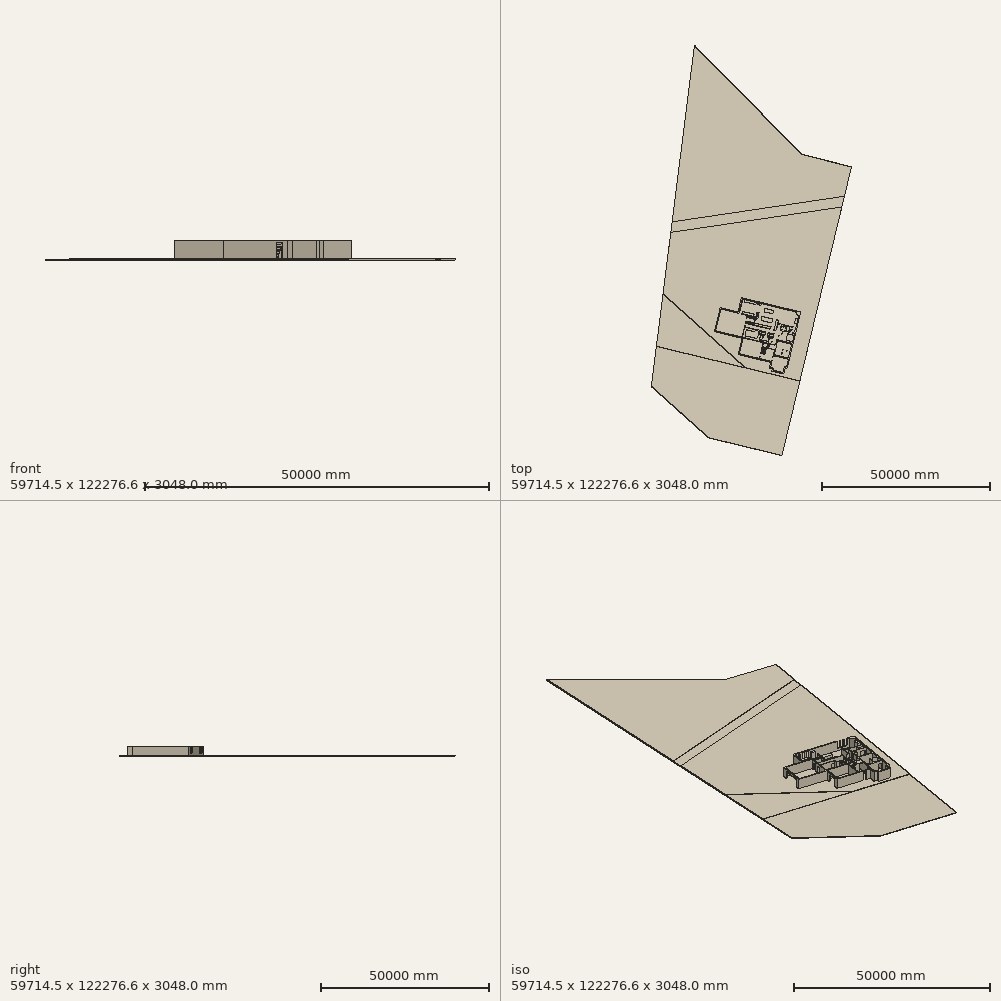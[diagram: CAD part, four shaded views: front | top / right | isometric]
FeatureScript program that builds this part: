
annotation { "Feature Type Name" : "Feature", "Feature Type Description" : "" }
export const myFeature = defineFeature(function(context is Context, id is Id, definition is map)
    precondition{}
    {
        {
            var Q0;
            Q0=qCreatedBy(makeId("Top.planeOp"),FACE);
            var sketch = newSketch(context, id + "F0", { "sketchPlane" : qUnion([Q0])});
            skLineSegment(sketch, "E0", {"start": v(0, 0) * mm, "end": v(31989.83, -32467.96) * mm});
            skLineSegment(sketch, "E1", {"start": v(31989.83, -32467.96) * mm, "end": v(46862.18, -36229.17) * mm});
            skLineSegment(sketch, "E2", {"start": v(46862.18, -36229.17) * mm, "end": v(26112.23, -122276.56) * mm});
            skLineSegment(sketch, "E3", {"start": v(46862.18, -36229.17) * mm, "end": v(46862.18, -51469.17) * mm, "construction": true});
            skLineSegment(sketch, "E4", {"start": v(0, 0) * mm, "end": v(-12852.3, -101676.89) * mm});
            skLineSegment(sketch, "E5", {"start": v(0, 0) * mm, "end": v(0, 15240) * mm, "construction": true});
            skLineSegment(sketch, "E6", {"start": v(26112.23, -122276.56) * mm, "end": v(4230, -116999.76) * mm});
            skLineSegment(sketch, "E7", {"start": v(26112.23, -122276.56) * mm, "end": v(10872.23, -122276.56) * mm, "construction": true});
            skLineSegment(sketch, "E8", {"start": v(4230, -116999.76) * mm, "end": v(-12852.3, -101676.89) * mm});
            skArc(sketch, "E9", {"start": v(-4165.07, -109469.35) * mm, "mid": v(-689.73, -114039.67) * mm, "end": v(4230, -116999.76) * mm, "construction": true});
            skArc(sketch, "E10", {"start": v(-4165.07, -109469.35) * mm, "mid": v(-8132.26, -105153.47) * mm, "end": v(-12852.3, -101676.89) * mm, "construction": true});
            skLineSegment(sketch, "E11", {"start": v(31471.2, -100053.58) * mm, "end": v(-11342.08, -89729.35) * mm});
            skLineSegment(sketch, "E12", {"start": v(-9365.85, -74095.03) * mm, "end": v(15198.72, -96129.54) * mm});
            skLineSegment(sketch, "E13", {"start": v(-6651.63, -52622.31) * mm, "end": v(44754.67, -44968.73) * mm});
            skLineSegment(sketch, "E14", {"start": v(-7048.63, -55763.02) * mm, "end": v(43983.88, -48165.09) * mm});
            skSolve(sketch);
        }
        {
            var Q0;
            {var subQ4=sQuery(id+"F0.wireOp",EDGE,"E0");Q0=makeQuery(id+"F0.imprint","IMPRINT",FACE,{"disambiguationData":[TD([[makeQuery(id+"F0.imprint","IMPRINT",EDGE,{"derivedFrom":subQ4}),-1.0]])]});}
            var Q1;
            {var subQ0=sQuery(id+"F0.wireOp",EDGE,"E13");Q1=makeQuery(id+"F0.imprint","IMPRINT",FACE,{"disambiguationData":[TD([[makeQuery(id+"F0.imprint","IMPRINT",EDGE,{"derivedFrom":subQ0}),-1.0]])]});}
            var Q2;
            {var subQ0=sQuery(id+"F0.wireOp",EDGE,"E12");Q2=makeQuery(id+"F0.imprint","IMPRINT",FACE,{"disambiguationData":[TD([[makeQuery(id+"F0.imprint","IMPRINT",EDGE,{"derivedFrom":subQ0}),1.0]])]});}
            var Q3;
            {var subQ3=sQuery(id+"F0.wireOp",EDGE,"E12");Q3=makeQuery(id+"F0.imprint","IMPRINT",FACE,{"disambiguationData":[TD([[makeQuery(id+"F0.imprint","IMPRINT",EDGE,{"derivedFrom":subQ3}),-1.0]])]});}
            var Q4;
            {var subQ1=sQuery(id+"F0.wireOp",EDGE,"E6");Q4=makeQuery(id+"F0.imprint","IMPRINT",FACE,{"disambiguationData":[TD([[makeQuery(id+"F0.imprint","IMPRINT",EDGE,{"derivedFrom":subQ1}),-1.0]])]});}
            extrude(context, id + "F1", {"entities" : qUnion([Q0, Q1, Q2, Q3, Q4]), "depth" : 304.8 * mm, "offsetDistance" : 25.4 * mm});
        }
        {
            var Q0;
            Q0=makeQuery(id+"F1.opExtrude","CAP_FACE",FACE,{"disambiguationData":[OSD([sQuery(id+"F0.wireOp",EDGE,"E0"),sQuery(id+"F0.wireOp",EDGE,"E1"),sQuery(id+"F0.wireOp",EDGE,"E2"),sQuery(id+"F0.wireOp",EDGE,"E4"),sQuery(id+"F0.wireOp",EDGE,"E6"),sQuery(id+"F0.wireOp",EDGE,"E8")])],"isStart":false});
            var sketch = newSketch(context, id + "F2", { "sketchPlane" : qUnion([Q0])});
            skLineSegment(sketch, "E15.0", {"start": v(-9365.85, -74095.03) * mm, "end": v(15198.72, -96129.54) * mm});
            skLineSegment(sketch, "E16.0", {"start": v(31471.2, -100053.58) * mm, "end": v(-11342.08, -89729.35) * mm});
            skLineSegment(sketch, "E17.0", {"start": v(0, 0) * mm, "end": v(-12852.3, -101676.89) * mm});
            skSolve(sketch);
        }
        {
            var Q0;
            {var subQ0=sQuery(id+"F2.wireOp",EDGE,"E15.0");Q0=makeQuery(id+"F2.imprint","IMPRINT",FACE,{"disambiguationData":[TD([[makeQuery(id+"F2.imprint","IMPRINT",EDGE,{"derivedFrom":subQ0}),-1.0]])]});}
            extrude(context, id + "F3", {"entities" : qUnion([Q0]), "operationType" : NewBodyOperationType.REMOVE, "oppositeDirection" : true, "depth" : 76.2 * mm, "offsetDistance" : 25.4 * mm});
        }
        {
            var Q0;
            Q0=makeQuery(id+"F1.opExtrude","CAP_FACE",FACE,{"disambiguationData":[OSD([sQuery(id+"F0.wireOp",EDGE,"E0"),sQuery(id+"F0.wireOp",EDGE,"E1"),sQuery(id+"F0.wireOp",EDGE,"E2"),sQuery(id+"F0.wireOp",EDGE,"E4"),sQuery(id+"F0.wireOp",EDGE,"E6"),sQuery(id+"F0.wireOp",EDGE,"E8")])],"isStart":false});
            var sketch = newSketch(context, id + "F4", { "sketchPlane" : qUnion([Q0])});
            skLineSegment(sketch, "E18.0", {"start": v(0, 0) * mm, "end": v(-12852.3, -101676.89) * mm});
            skLineSegment(sketch, "E19.0", {"start": v(4230, -116999.76) * mm, "end": v(-12852.3, -101676.89) * mm});
            skLineSegment(sketch, "E20.0", {"start": v(26112.23, -122276.56) * mm, "end": v(4230, -116999.76) * mm});
            skLineSegment(sketch, "E21.0", {"start": v(46862.18, -36229.17) * mm, "end": v(26112.23, -122276.56) * mm});
            skLineSegment(sketch, "E22.0", {"start": v(31471.2, -100053.58) * mm, "end": v(-11342.08, -89729.35) * mm});
            skSolve(sketch);
        }
        {
            var Q0;
            {var subQ4=sQuery(id+"F4.wireOp",EDGE,"E19.0");Q0=makeQuery(id+"F4.imprint","IMPRINT",FACE,{"disambiguationData":[TD([[makeQuery(id+"F4.imprint","IMPRINT",EDGE,{"derivedFrom":subQ4}),-1.0]])]});}
            extrude(context, id + "F5", {"entities" : qUnion([Q0]), "operationType" : NewBodyOperationType.REMOVE, "oppositeDirection" : true, "depth" : 152.4 * mm, "offsetDistance" : 25.4 * mm});
        }
        {
            var Q0;
            Q0=makeQuery(id+"F1.opExtrude","CAP_FACE",FACE,{"disambiguationData":[OSD([sQuery(id+"F0.wireOp",EDGE,"E0"),sQuery(id+"F0.wireOp",EDGE,"E1"),sQuery(id+"F0.wireOp",EDGE,"E2"),sQuery(id+"F0.wireOp",EDGE,"E4"),sQuery(id+"F0.wireOp",EDGE,"E6"),sQuery(id+"F0.wireOp",EDGE,"E8")])],"isStart":false});
            var sketch = newSketch(context, id + "F6", { "sketchPlane" : qUnion([Q0])});
            skLineSegment(sketch, "E23.0", {"start": v(-6651.63, -52622.31) * mm, "end": v(44754.67, -44968.73) * mm});
            skLineSegment(sketch, "E24.0", {"start": v(-7048.63, -55763.02) * mm, "end": v(43983.88, -48165.09) * mm});
            skLineSegment(sketch, "E25.0", {"start": v(0, 0) * mm, "end": v(-12852.3, -101676.89) * mm});
            skLineSegment(sketch, "E26.0", {"start": v(46862.18, -36229.17) * mm, "end": v(26112.23, -122276.56) * mm});
            skSolve(sketch);
        }
        {
            var Q0;
            {var subQ0=sQuery(id+"F6.wireOp",EDGE,"E23.0");Q0=makeQuery(id+"F6.imprint","IMPRINT",FACE,{"disambiguationData":[TD([[makeQuery(id+"F6.imprint","IMPRINT",EDGE,{"derivedFrom":subQ0}),-1.0]])]});}
            extrude(context, id + "F7", {"entities" : qUnion([Q0]), "operationType" : NewBodyOperationType.REMOVE, "oppositeDirection" : true, "depth" : 152.4 * mm, "offsetDistance" : 25.4 * mm});
        }
        {
            var Q0;
            {var subQ0=sQuery(id+"F0.wireOp",EDGE,"E4");var subQ1=sQuery(id+"F0.wireOp",EDGE,"E2");Q0=makeQuery(id+"F7.boolean.opBoolean","SPLIT",FACE,{"disambiguationData":[TD([makeQuery(id+"F3.boolean.opBoolean","COPY",FACE,{"derivedFrom":makeQuery(id+"F3.opExtrude","SWEPT_FACE",FACE,{"disambiguationData":[OSD([sQuery(id+"F2.wireOp",EDGE,"E15.0")])]})})])],"derivedFrom":makeQuery(id+"F1.opExtrude","CAP_FACE",FACE,{"disambiguationData":[OSD([sQuery(id+"F0.wireOp",EDGE,"E0"),sQuery(id+"F0.wireOp",EDGE,"E1"),subQ1,subQ0,sQuery(id+"F0.wireOp",EDGE,"E6"),sQuery(id+"F0.wireOp",EDGE,"E8")])],"isStart":false})});}
            var sketch = newSketch(context, id + "F8", { "sketchPlane" : qUnion([Q0])});
            skLineSegment(sketch, "E27", {"start": v(27669.68, -96315.03) * mm, "end": v(31724.64, -79499.64) * mm});
            skPoint(sketch, "E28.orphan", {"position": v(31471.2, -100053.58) * mm});
            skLineSegment(sketch, "E29", {"start": v(-5717.12, -79311.3) * mm, "end": v(3764.68, -81597.8) * mm});
            skLineSegment(sketch, "E30", {"start": v(3764.68, -81597.8) * mm, "end": v(7766.05, -65004.64) * mm});
            skLineSegment(sketch, "E31", {"start": v(7766.05, -65004.64) * mm, "end": v(-1715.76, -62718.14) * mm});
            skLineSegment(sketch, "E32", {"start": v(-1715.76, -62718.14) * mm, "end": v(-5717.12, -79311.3) * mm});
            skLineSegment(sketch, "E33", {"start": v(-5145.5, -76940.85) * mm, "end": v(-2182.44, -77655.38) * mm});
            skLineSegment(sketch, "E34", {"start": v(-2182.44, -77655.38) * mm, "end": v(-2754.06, -80025.83) * mm});
            skLineSegment(sketch, "E35", {"start": v(-5145.5, -76940.85) * mm, "end": v(-9590.1, -75869.05) * mm});
            skLineSegment(sketch, "E36", {"start": v(-2182.44, -77655.38) * mm, "end": v(1247.3, -63432.67) * mm});
            skLineSegment(sketch, "E37", {"start": v(3764.68, -81597.8) * mm, "end": v(7190.64, -82423.95) * mm});
            skLineSegment(sketch, "E38", {"start": v(4934.3, -91780.7) * mm, "end": v(-10343.91, -88096.42) * mm});
            skLineSegment(sketch, "E39.0", {"start": v(4230, -116999.76) * mm, "end": v(-12852.3, -101676.89) * mm});
            skLineSegment(sketch, "E40", {"start": v(-2047.33, -90097.1) * mm, "end": v(-6264.7, -107585.98) * mm});
            skLineSegment(sketch, "E41", {"start": v(-5603, -89239.67) * mm, "end": v(-9358.03, -104811.25) * mm});
            skArc(sketch, "E42", {"start": v(-6746.26, -93980.57) * mm, "mid": v(-7326.44, -90293.4) * mm, "end": v(-10343.91, -88096.42) * mm});
            skLineSegment(sketch, "E43", {"start": v(-8087.58, -78739.68) * mm, "end": v(-10343.91, -88096.42) * mm});
            skLineSegment(sketch, "E44", {"start": v(-5717.12, -79311.3) * mm, "end": v(-8087.58, -78739.68) * mm});
            skLineSegment(sketch, "E45", {"start": v(22775.38, -94507.71) * mm, "end": v(22346.66, -96285.55) * mm});
            skLineSegment(sketch, "E46", {"start": v(22346.66, -96285.55) * mm, "end": v(23235.58, -96499.91) * mm});
            skLineSegment(sketch, "E47", {"start": v(23235.58, -96499.91) * mm, "end": v(23092.67, -97092.52) * mm});
            skLineSegment(sketch, "E48", {"start": v(23092.67, -97092.52) * mm, "end": v(26648.35, -97949.96) * mm});
            skLineSegment(sketch, "E49", {"start": v(26648.35, -97949.96) * mm, "end": v(27077.07, -96172.12) * mm});
            skLineSegment(sketch, "E50", {"start": v(13071.34, -92167.63) * mm, "end": v(14241.39, -87315.61) * mm});
            skLineSegment(sketch, "E51", {"start": v(14241.39, -87315.61) * mm, "end": v(5985.04, -85324.63) * mm});
            skLineSegment(sketch, "E52", {"start": v(5985.04, -85324.63) * mm, "end": v(7699.91, -78213.28) * mm});
            skLineSegment(sketch, "E53", {"start": v(14020.33, -75230.32) * mm, "end": v(31724.64, -79499.64) * mm});
            skLineSegment(sketch, "E54.trimOffspring", {"start": v(27077.07, -96172.12) * mm, "end": v(27669.68, -96315.03) * mm});
            skLineSegment(sketch, "E55.0", {"start": v(6352.8, -85099.78) * mm, "end": v(7924.77, -78581.03) * mm});
            skLineSegment(sketch, "E55.1", {"start": v(23460.43, -96867.67) * mm, "end": v(26423.5, -97582.2) * mm});
            skLineSegment(sketch, "E55.2", {"start": v(26423.5, -97582.2) * mm, "end": v(26852.22, -95804.36) * mm});
            skLineSegment(sketch, "E55.3", {"start": v(26852.22, -95804.36) * mm, "end": v(27444.83, -95947.27) * mm});
            skLineSegment(sketch, "E55.4", {"start": v(27444.83, -95947.27) * mm, "end": v(28016.45, -93576.82) * mm});
            skLineSegment(sketch, "E55.5", {"start": v(23603.34, -96275.06) * mm, "end": v(23460.43, -96867.67) * mm});
            skLineSegment(sketch, "E55.6", {"start": v(14245.18, -75598.08) * mm, "end": v(19282.4, -76812.78) * mm});
            skLineSegment(sketch, "E55.7", {"start": v(22714.42, -96060.7) * mm, "end": v(23603.34, -96275.06) * mm});
            skLineSegment(sketch, "E55.8", {"start": v(23143.14, -94282.86) * mm, "end": v(22714.42, -96060.7) * mm});
            skLineSegment(sketch, "E55.9", {"start": v(13439.1, -91942.77) * mm, "end": v(23143.14, -94282.86) * mm});
            skLineSegment(sketch, "E55.10", {"start": v(13439.1, -91942.77) * mm, "end": v(14609.14, -87090.76) * mm});
            skLineSegment(sketch, "E55.11", {"start": v(14609.14, -87090.76) * mm, "end": v(6352.8, -85099.78) * mm});
            skLineSegment(sketch, "E56", {"start": v(14609.14, -87090.76) * mm, "end": v(19350.05, -88234) * mm});
            skLineSegment(sketch, "E57", {"start": v(20619.6, -88657.73) * mm, "end": v(19476.35, -93398.63) * mm});
            skLineSegment(sketch, "E58.0", {"start": v(20508.48, -88630.93) * mm, "end": v(19365.23, -93371.83) * mm});
            skLineSegment(sketch, "E58.1", {"start": v(14582.35, -87201.87) * mm, "end": v(20508.48, -88630.93) * mm});
            skLineSegment(sketch, "E59", {"start": v(17710.43, -83331.52) * mm, "end": v(18255.26, -81072.19) * mm});
            skLineSegment(sketch, "E60", {"start": v(17821.54, -83358.32) * mm, "end": v(18393.17, -80987.87) * mm});
            skLineSegment(sketch, "E61", {"start": v(7924.77, -78581.03) * mm, "end": v(18255.26, -81072.19) * mm});
            skLineSegment(sketch, "E62", {"start": v(14020.33, -75230.32) * mm, "end": v(12993.2, -79489.73) * mm});
            skLineSegment(sketch, "E63", {"start": v(12993.2, -79489.73) * mm, "end": v(7699.91, -78213.28) * mm});
            skLineSegment(sketch, "E64", {"start": v(14245.18, -75598.08) * mm, "end": v(13218.05, -79857.49) * mm});
            skLineSegment(sketch, "E65", {"start": v(13244.84, -79746.37) * mm, "end": v(18393.17, -80987.87) * mm});
            skLineSegment(sketch, "E66", {"start": v(23143.14, -94282.86) * mm, "end": v(23571.86, -92505.02) * mm});
            skLineSegment(sketch, "E67", {"start": v(24202.07, -89404.05) * mm, "end": v(19350.05, -88234) * mm});
            skLineSegment(sketch, "E68", {"start": v(23032.02, -94256.07) * mm, "end": v(24175.27, -89515.16) * mm});
            skLineSegment(sketch, "E69", {"start": v(24175.27, -89515.16) * mm, "end": v(20619.6, -88657.73) * mm});
            skLineSegment(sketch, "E70", {"start": v(19833.61, -91917.1) * mm, "end": v(21018.84, -92202.9) * mm});
            skLineSegment(sketch, "E71", {"start": v(21018.84, -92202.9) * mm, "end": v(21519, -90128.76) * mm});
            skLineSegment(sketch, "E72", {"start": v(21519, -90128.76) * mm, "end": v(23889.46, -90700.39) * mm});
            skLineSegment(sketch, "E73", {"start": v(23571.86, -92505.02) * mm, "end": v(28016.45, -93576.82) * mm});
            skLineSegment(sketch, "E74", {"start": v(23828.5, -92253.37) * mm, "end": v(27982.96, -93255.2) * mm});
            skLineSegment(sketch, "E75", {"start": v(28983.3, -89106.91) * mm, "end": v(24828.84, -88105.08) * mm});
            skLineSegment(sketch, "E76", {"start": v(27982.96, -93255.2) * mm, "end": v(28983.3, -89106.91) * mm});
            skLineSegment(sketch, "E77", {"start": v(23828.5, -92253.37) * mm, "end": v(24828.84, -88105.08) * mm});
            skLineSegment(sketch, "E78.trimOffspring", {"start": v(29159.7, -88835.91) * mm, "end": v(31356.88, -79724.5) * mm});
            skLineSegment(sketch, "E79", {"start": v(29159.7, -88835.91) * mm, "end": v(24603.99, -87737.32) * mm});
            skLineSegment(sketch, "E80", {"start": v(24603.99, -87737.32) * mm, "end": v(24202.07, -89404.05) * mm});
            skLineSegment(sketch, "E81", {"start": v(25201.65, -81845.86) * mm, "end": v(24951.57, -82882.93) * mm});
            skLineSegment(sketch, "E82", {"start": v(24951.57, -82882.93) * mm, "end": v(30285.09, -84169.09) * mm});
            skLineSegment(sketch, "E83", {"start": v(25090.54, -81819.07) * mm, "end": v(24340.28, -84930.28) * mm});
            skLineSegment(sketch, "E84", {"start": v(24924.77, -82994.05) * mm, "end": v(30258.3, -84280.2) * mm});
            skLineSegment(sketch, "E85", {"start": v(21057.5, -78390.48) * mm, "end": v(23724.26, -79033.55) * mm});
            skLineSegment(sketch, "E86", {"start": v(23724.26, -79033.55) * mm, "end": v(23474.18, -80070.63) * mm});
            skLineSegment(sketch, "E87", {"start": v(23474.18, -80070.63) * mm, "end": v(20807.42, -79427.55) * mm});
            skLineSegment(sketch, "E88", {"start": v(20807.42, -79427.55) * mm, "end": v(21057.5, -78390.48) * mm});
            skLineSegment(sketch, "E89", {"start": v(12993.2, -79489.73) * mm, "end": v(12921.74, -79786.03) * mm});
            skLineSegment(sketch, "E90", {"start": v(17821.54, -83358.32) * mm, "end": v(24340.28, -84930.28) * mm});
            skLineSegment(sketch, "E91", {"start": v(25961.85, -83244.13) * mm, "end": v(25553.97, -84935.55) * mm});
            skLineSegment(sketch, "E92", {"start": v(15313.18, -82871.01) * mm, "end": v(24424.6, -85068.2) * mm});
            skLineSegment(sketch, "E93", {"start": v(24424.6, -85068.2) * mm, "end": v(24924.77, -82994.05) * mm});
            skLineSegment(sketch, "E94", {"start": v(25054.81, -81967.22) * mm, "end": v(24462.2, -81824.31) * mm});
            skLineSegment(sketch, "E95", {"start": v(24462.2, -81824.31) * mm, "end": v(23747.67, -84787.38) * mm});
            skLineSegment(sketch, "E96", {"start": v(22853.5, -83944.68) * mm, "end": v(17964.45, -82765.7) * mm});
            skLineSegment(sketch, "E97", {"start": v(18807.15, -81871.54) * mm, "end": v(19343.04, -79649.24) * mm});
            skLineSegment(sketch, "E98", {"start": v(20165.76, -80788.24) * mm, "end": v(19879.94, -81973.47) * mm});
            skLineSegment(sketch, "E99", {"start": v(19879.94, -81973.47) * mm, "end": v(23139.32, -82759.45) * mm});
            skLineSegment(sketch, "E100", {"start": v(23139.32, -82759.45) * mm, "end": v(23425.13, -81574.23) * mm});
            skLineSegment(sketch, "E101", {"start": v(23425.13, -81574.23) * mm, "end": v(20165.76, -80788.24) * mm});
            skLineSegment(sketch, "E102", {"start": v(19282.4, -76812.78) * mm, "end": v(25912.25, -78411.54) * mm});
            skLineSegment(sketch, "E103.trimOffspring", {"start": v(26023.36, -78438.34) * mm, "end": v(31356.88, -79724.5) * mm});
            skLineSegment(sketch, "E104", {"start": v(27837.43, -93533.65) * mm, "end": v(27908.89, -93237.34) * mm});
            skLineSegment(sketch, "E105", {"start": v(26948.51, -93319.29) * mm, "end": v(27019.97, -93022.98) * mm});
            skLineSegment(sketch, "E106", {"start": v(26972.33, -93220.52) * mm, "end": v(27861.25, -93434.88) * mm});
            skLineSegment(sketch, "E107", {"start": v(26963.4, -93257.56) * mm, "end": v(27852.32, -93471.92) * mm});
            skLineSegment(sketch, "E108", {"start": v(24810.98, -88179.16) * mm, "end": v(24514.67, -88107.7) * mm});
            skLineSegment(sketch, "E109", {"start": v(24300.31, -88996.63) * mm, "end": v(24596.62, -89068.08) * mm});
            skLineSegment(sketch, "E110", {"start": v(24362.04, -89011.51) * mm, "end": v(24576.4, -88122.6) * mm});
            skLineSegment(sketch, "E111", {"start": v(24399.08, -89020.44) * mm, "end": v(24613.44, -88131.52) * mm});
            skLineSegment(sketch, "E112", {"start": v(23016.84, -89118.24) * mm, "end": v(23543.8, -86932.98) * mm});
            skLineSegment(sketch, "E113", {"start": v(22905.73, -89091.44) * mm, "end": v(23405.9, -87017.3) * mm});
            skLineSegment(sketch, "E114", {"start": v(15884.8, -80500.56) * mm, "end": v(14312.84, -87019.3) * mm});
            skLineSegment(sketch, "E115", {"start": v(15339.97, -82759.9) * mm, "end": v(17710.43, -83331.52) * mm});
            skLineSegment(sketch, "E116", {"start": v(18807.15, -81871.54) * mm, "end": v(18214.53, -81728.63) * mm});
            skLineSegment(sketch, "E117", {"start": v(13071.34, -92167.63) * mm, "end": v(23071.68, -94579.17) * mm});
            skLineSegment(sketch, "E118", {"start": v(19247.36, -85896.9) * mm, "end": v(23543.8, -86932.98) * mm});
            skLineSegment(sketch, "E119", {"start": v(19109.45, -85981.23) * mm, "end": v(19739.1, -86133.06) * mm});
            skLineSegment(sketch, "E120", {"start": v(22016.8, -88877.08) * mm, "end": v(22516.98, -86802.94) * mm});
            skLineSegment(sketch, "E121", {"start": v(21905.7, -88850.29) * mm, "end": v(22405.86, -86776.14) * mm});
            skLineSegment(sketch, "E122", {"start": v(20090.81, -88412.64) * mm, "end": v(20590.98, -86338.5) * mm});
            skLineSegment(sketch, "E123", {"start": v(20201.93, -88439.43) * mm, "end": v(20702.1, -86365.29) * mm});
            skLineSegment(sketch, "E124", {"start": v(20344.83, -87846.82) * mm, "end": v(22048.6, -88257.67) * mm});
            skCircle(sketch, "E125", {"center": v(20717.84, -88250.3) * mm, "radius": 152.4 * mm});
            skCircle(sketch, "E126", {"center": v(21532.68, -88446.8) * mm, "radius": 152.4 * mm});
            skLineSegment(sketch, "E127", {"start": v(19473.5, -88263.78) * mm, "end": v(19544.96, -87967.47) * mm});
            skLineSegment(sketch, "E128", {"start": v(19544.96, -87967.47) * mm, "end": v(20038.8, -88086.56) * mm});
            skLineSegment(sketch, "E129", {"start": v(20038.8, -88086.56) * mm, "end": v(19967.35, -88382.87) * mm});
            skLineSegment(sketch, "E130", {"start": v(19643.73, -87991.29) * mm, "end": v(19756.86, -87522.14) * mm});
            skLineSegment(sketch, "E131", {"start": v(19756.86, -87522.14) * mm, "end": v(20053.17, -87593.59) * mm});
            skLineSegment(sketch, "E132", {"start": v(20053.17, -87593.59) * mm, "end": v(19940.04, -88062.74) * mm});
            skLineSegment(sketch, "E133", {"start": v(19760.9, -86530.24) * mm, "end": v(20501.67, -86708.88) * mm});
            skLineSegment(sketch, "E134", {"start": v(20600.87, -86785.05) * mm, "end": v(20489.76, -86758.26) * mm});
            skLineSegment(sketch, "E135", {"start": v(20346.85, -87350.87) * mm, "end": v(20457.97, -87377.67) * mm});
            skLineSegment(sketch, "E136", {"start": v(20402.41, -87364.27) * mm, "end": v(20545.32, -86771.66) * mm});
            skArc(sketch, "E137", {"start": v(20402.41, -87364.27) * mm, "mid": v(20012.42, -87067.68) * mm, "end": v(19966.67, -86579.86) * mm, "construction": true});
            skLineSegment(sketch, "E138", {"start": v(22231.16, -87988.16) * mm, "end": v(23120.08, -88202.52) * mm});
            skLineSegment(sketch, "E139", {"start": v(23120.08, -88202.52) * mm, "end": v(22016.8, -88877.08) * mm});
            skLineSegment(sketch, "E140", {"start": v(22231.16, -87988.16) * mm, "end": v(22905.73, -89091.44) * mm});
            skCircle(sketch, "E141", {"center": v(22568.44, -88539.8) * mm, "radius": 50.8 * mm});
            skLineSegment(sketch, "E142", {"start": v(22427.66, -87173.32) * mm, "end": v(23316.58, -87387.68) * mm});
            skLineSegment(sketch, "E143", {"start": v(22304.64, -87195.9) * mm, "end": v(22415.75, -87222.7) * mm});
            skLineSegment(sketch, "E144", {"start": v(22161.73, -87788.52) * mm, "end": v(22272.85, -87815.32) * mm});
            skLineSegment(sketch, "E145", {"start": v(22360.2, -87209.3) * mm, "end": v(22217.29, -87801.92) * mm});
            skArc(sketch, "E146", {"start": v(22217.29, -87801.92) * mm, "mid": v(22699.6, -87715.68) * mm, "end": v(22962.65, -87302.33) * mm, "construction": true});
            skLineSegment(sketch, "E147", {"start": v(19461.72, -85007.99) * mm, "end": v(21239.56, -85436.7) * mm});
            skLineSegment(sketch, "E148", {"start": v(19390.27, -85304.3) * mm, "end": v(21168.1, -85733.01) * mm});
            skLineSegment(sketch, "E149", {"start": v(20612.78, -86735.67) * mm, "end": v(20909.09, -86807.12) * mm});
            skLineSegment(sketch, "E150", {"start": v(21239.56, -85436.7) * mm, "end": v(21025.2, -86325.63) * mm});
            skLineSegment(sketch, "E151", {"start": v(21980.33, -85615.34) * mm, "end": v(21765.97, -86504.26) * mm});
            skLineSegment(sketch, "E152", {"start": v(21099.28, -86343.49) * mm, "end": v(21072.48, -86454.6) * mm});
            skLineSegment(sketch, "E153", {"start": v(21691.9, -86486.4) * mm, "end": v(21665.1, -86597.5) * mm});
            skLineSegment(sketch, "E154", {"start": v(21085.88, -86399.05) * mm, "end": v(21678.5, -86541.95) * mm});
            skLineSegment(sketch, "E155", {"start": v(20909.09, -86807.12) * mm, "end": v(20998.4, -86436.74) * mm});
            skLineSegment(sketch, "E156", {"start": v(21649.86, -86985.76) * mm, "end": v(21739.17, -86615.37) * mm});
            skLineSegment(sketch, "E157.trimOffspring", {"start": v(21649.86, -86985.76) * mm, "end": v(22316.55, -87146.52) * mm});
            skLineSegment(sketch, "E158.trimOffspring", {"start": v(21908.87, -85911.64) * mm, "end": v(23686.71, -86340.36) * mm});
            skLineSegment(sketch, "E159.trimOffspring", {"start": v(21980.33, -85615.34) * mm, "end": v(23758.16, -86044.06) * mm});
            skLineSegment(sketch, "E160", {"start": v(15482.88, -82167.29) * mm, "end": v(17853.33, -82738.9) * mm});
            skLineSegment(sketch, "E161", {"start": v(15741.9, -81093.17) * mm, "end": v(18112.35, -81664.8) * mm});
            skLineSegment(sketch, "E162", {"start": v(17889.06, -82590.76) * mm, "end": v(18000.17, -82617.55) * mm});
            skLineSegment(sketch, "E163", {"start": v(18067.7, -81850) * mm, "end": v(18178.8, -81876.79) * mm});
            skLineSegment(sketch, "E164", {"start": v(18123.25, -81863.39) * mm, "end": v(17944.62, -82604.15) * mm});
            skLineSegment(sketch, "E165", {"start": v(15397.07, -82035.55) * mm, "end": v(15508.19, -82062.34) * mm});
            skLineSegment(sketch, "E166", {"start": v(15611.43, -81146.63) * mm, "end": v(15722.55, -81173.42) * mm});
            skLineSegment(sketch, "E167", {"start": v(15666.99, -81160.03) * mm, "end": v(15452.63, -82048.95) * mm});
            skLineSegment(sketch, "E168", {"start": v(22853.5, -83944.68) * mm, "end": v(22710.6, -84537.3) * mm});
            skLineSegment(sketch, "E169", {"start": v(22784.67, -84555.16) * mm, "end": v(22757.88, -84666.27) * mm});
            skLineSegment(sketch, "E170", {"start": v(23673.6, -84769.51) * mm, "end": v(23646.8, -84880.63) * mm});
            skLineSegment(sketch, "E171", {"start": v(26072.96, -83270.93) * mm, "end": v(25665.08, -84962.34) * mm});
            skLineSegment(sketch, "E172", {"start": v(25715.7, -84752.46) * mm, "end": v(29901.03, -85761.73) * mm});
            skLineSegment(sketch, "E173", {"start": v(25688.9, -84863.58) * mm, "end": v(29874.23, -85872.85) * mm});
            skLineSegment(sketch, "E174", {"start": v(28554.53, -83869.35) * mm, "end": v(28197.26, -85350.88) * mm});
            skLineSegment(sketch, "E175", {"start": v(28443.41, -83842.55) * mm, "end": v(28086.15, -85324.08) * mm});
            skLineSegment(sketch, "E176", {"start": v(27702.65, -83663.92) * mm, "end": v(27345.38, -85145.45) * mm});
            skLineSegment(sketch, "E177", {"start": v(25941.96, -83814.16) * mm, "end": v(26830.88, -84028.52) * mm});
            skLineSegment(sketch, "E178", {"start": v(26830.88, -84028.52) * mm, "end": v(26961.88, -83485.29) * mm});
            skLineSegment(sketch, "E179", {"start": v(27085.34, -83515.06) * mm, "end": v(27013.89, -83811.37) * mm});
            skLineSegment(sketch, "E180", {"start": v(27013.89, -83811.37) * mm, "end": v(27507.73, -83930.45) * mm});
            skLineSegment(sketch, "E181", {"start": v(27507.73, -83930.45) * mm, "end": v(27579.19, -83634.15) * mm});
            skLineSegment(sketch, "E182", {"start": v(27112.66, -83835.18) * mm, "end": v(26999.52, -84304.34) * mm});
            skLineSegment(sketch, "E183", {"start": v(26999.52, -84304.34) * mm, "end": v(27295.83, -84375.79) * mm});
            skLineSegment(sketch, "E184", {"start": v(27295.83, -84375.79) * mm, "end": v(27408.96, -83906.64) * mm});
            skLineSegment(sketch, "E185", {"start": v(25762.98, -84881.44) * mm, "end": v(25789.77, -84770.32) * mm});
            skLineSegment(sketch, "E186", {"start": v(26355.6, -85024.34) * mm, "end": v(26382.39, -84913.23) * mm});
            skLineSegment(sketch, "E187", {"start": v(25776.38, -84825.88) * mm, "end": v(26368.99, -84968.79) * mm});
            skArc(sketch, "E188", {"start": v(26368.99, -84968.79) * mm, "mid": v(26275.53, -84475.95) * mm, "end": v(25844.08, -84220.05) * mm, "construction": true});
            skLineSegment(sketch, "E189", {"start": v(28340.17, -84758.27) * mm, "end": v(30043.93, -85169.12) * mm});
            skLineSegment(sketch, "E190", {"start": v(28366.96, -84647.15) * mm, "end": v(30070.73, -85058) * mm});
            skLineSegment(sketch, "E191", {"start": v(29278.79, -88342.07) * mm, "end": v(27303.41, -87865.72) * mm});
            skLineSegment(sketch, "E192", {"start": v(27303.41, -87865.72) * mm, "end": v(27755.95, -85989.1) * mm});
            skLineSegment(sketch, "E193", {"start": v(27755.95, -85989.1) * mm, "end": v(29731.32, -86465.46) * mm});
            skLineSegment(sketch, "E194", {"start": v(28296.03, -85374.7) * mm, "end": v(28269.24, -85485.81) * mm});
            skLineSegment(sketch, "E195", {"start": v(29777.56, -85731.96) * mm, "end": v(29750.77, -85843.08) * mm});
            skLineSegment(sketch, "E196", {"start": v(29036.8, -85553.33) * mm, "end": v(29010, -85664.44) * mm});
            skLineSegment(sketch, "E197", {"start": v(28282.63, -85430.25) * mm, "end": v(29023.4, -85608.89) * mm});
            skLineSegment(sketch, "E198", {"start": v(29023.4, -85608.89) * mm, "end": v(29764.17, -85787.52) * mm});
            skArc(sketch, "E199", {"start": v(25137.16, -86664) * mm, "mid": v(24733.67, -87037.01) * mm, "end": v(24922.8, -87552.92) * mm});
            skLineSegment(sketch, "E200", {"start": v(26429.67, -85042.2) * mm, "end": v(26197.45, -86005.2) * mm});
            skLineSegment(sketch, "E201", {"start": v(26197.45, -86005.2) * mm, "end": v(25456.68, -85826.57) * mm});
            skLineSegment(sketch, "E202", {"start": v(26540.78, -85069) * mm, "end": v(26281.77, -86143.11) * mm});
            skLineSegment(sketch, "E203", {"start": v(26281.77, -86143.11) * mm, "end": v(25429.88, -85937.69) * mm});
            skLineSegment(sketch, "E204", {"start": v(26405.85, -85140.98) * mm, "end": v(26516.97, -85167.77) * mm});
            skLineSegment(sketch, "E205", {"start": v(26215.3, -85931.13) * mm, "end": v(26326.42, -85957.92) * mm});
            skLineSegment(sketch, "E206", {"start": v(26461.4, -85154.37) * mm, "end": v(26270.87, -85944.52) * mm});
            skArc(sketch, "E207", {"start": v(26270.87, -85944.52) * mm, "mid": v(26927.99, -85819.92) * mm, "end": v(27269.18, -85244.65) * mm, "construction": true});
            skLineSegment(sketch, "E208", {"start": v(25363.43, -85725.7) * mm, "end": v(25474.54, -85752.5) * mm});
            skLineSegment(sketch, "E209", {"start": v(25553.97, -84935.55) * mm, "end": v(25665.08, -84962.34) * mm});
            skLineSegment(sketch, "E210.trimOffspring", {"start": v(25363.43, -85725.7) * mm, "end": v(24863.26, -87799.85) * mm});
            skLineSegment(sketch, "E211.trimOffspring", {"start": v(25474.54, -85752.5) * mm, "end": v(24974.37, -87826.64) * mm});
            skLineSegment(sketch, "E212", {"start": v(24733.67, -87037.01) * mm, "end": v(25029.98, -87108.46) * mm, "construction": true});
            skLineSegment(sketch, "E213", {"start": v(23543.8, -86932.98) * mm, "end": v(23758.16, -86044.06) * mm});
            skLineSegment(sketch, "E214", {"start": v(20717.84, -88250.3) * mm, "end": v(21532.68, -88446.8) * mm, "construction": true});
            skLineSegment(sketch, "E215", {"start": v(14201.72, -86992.5) * mm, "end": v(15773.69, -80473.77) * mm});
            skLineSegment(sketch, "E216", {"start": v(15063.1, -83908.09) * mm, "end": v(19470.65, -84970.95) * mm});
            skLineSegment(sketch, "E217", {"start": v(19739.1, -86133.06) * mm, "end": v(19238.93, -88207.2) * mm});
            skLineSegment(sketch, "E218", {"start": v(19470.65, -84970.95) * mm, "end": v(19247.36, -85896.9) * mm});
            skLineSegment(sketch, "E219.trimOffspring", {"start": v(19850.22, -86159.86) * mm, "end": v(19350.05, -88234) * mm});
            skLineSegment(sketch, "E220.trimOffspring", {"start": v(19850.22, -86159.86) * mm, "end": v(23405.9, -87017.3) * mm});
            skLineSegment(sketch, "E221", {"start": v(15036.3, -84019.2) * mm, "end": v(19332.74, -85055.27) * mm});
            skLineSegment(sketch, "E222", {"start": v(19332.74, -85055.27) * mm, "end": v(19109.45, -85981.23) * mm});
            skLineSegment(sketch, "E223", {"start": v(23000.54, -90486.03) * mm, "end": v(23286.35, -89300.8) * mm});
            skLineSegment(sketch, "E224", {"start": v(20809.72, -93720.17) * mm, "end": v(20738.27, -94016.47) * mm});
            skLineSegment(sketch, "E225", {"start": v(21698.64, -93934.53) * mm, "end": v(21627.2, -94230.83) * mm});
            skLineSegment(sketch, "E226", {"start": v(20774, -93868.32) * mm, "end": v(21662.92, -94082.68) * mm});
            skLineSegment(sketch, "E227", {"start": v(18295.67, -84805.18) * mm, "end": v(18152.76, -85397.8) * mm});
            skLineSegment(sketch, "E228", {"start": v(18152.76, -85397.8) * mm, "end": v(15486, -84754.72) * mm});
            skLineSegment(sketch, "E229", {"start": v(15486, -84754.72) * mm, "end": v(15048.36, -86569.6) * mm});
            skLineSegment(sketch, "E230", {"start": v(15048.36, -86569.6) * mm, "end": v(18789.23, -87471.7) * mm});
            skLineSegment(sketch, "E231", {"start": v(18789.23, -87471.7) * mm, "end": v(19146.5, -85990.16) * mm});
            skLineSegment(sketch, "E232", {"start": v(18396.54, -84711.93) * mm, "end": v(18369.75, -84823.05) * mm});
            skLineSegment(sketch, "E233", {"start": v(19285.46, -84926.3) * mm, "end": v(19258.67, -85037.4) * mm});
            skLineSegment(sketch, "E234", {"start": v(18383.14, -84767.49) * mm, "end": v(19272.06, -84981.85) * mm});
            skArc(sketch, "E235", {"start": v(18383.14, -84767.49) * mm, "mid": v(18512.5, -85490.95) * mm, "end": v(19132.53, -85885.54) * mm, "construction": true});
            skArc(sketch, "E236", {"start": v(24399.08, -89020.44) * mm, "mid": v(25122.55, -88891.09) * mm, "end": v(25517.13, -88271.06) * mm, "construction": true});
            skArc(sketch, "E237", {"start": v(26972.33, -93220.52) * mm, "mid": v(27417.21, -92635.53) * mm, "end": v(28148.94, -92566.91) * mm, "construction": true});
            skArc(sketch, "E238", {"start": v(21678.5, -86541.95) * mm, "mid": v(21370.68, -86938.03) * mm, "end": v(20870.02, -86969.15) * mm, "construction": true});
            skLineSegment(sketch, "E239", {"start": v(28435.5, -91378.6) * mm, "end": v(27052.74, -91045.15) * mm});
            skLineSegment(sketch, "E240", {"start": v(26412.84, -90773.26) * mm, "end": v(25933.51, -92760.99) * mm});
            skLineSegment(sketch, "E241", {"start": v(25822.4, -92734.2) * mm, "end": v(26301.73, -90746.47) * mm});
            skLineSegment(sketch, "E242", {"start": v(27079.53, -90934.03) * mm, "end": v(28462.3, -91267.48) * mm});
            skLineSegment(sketch, "E243", {"start": v(27872.16, -88838.96) * mm, "end": v(27401.76, -90789.65) * mm});
            skLineSegment(sketch, "E244", {"start": v(27401.76, -90789.65) * mm, "end": v(28512.9, -91057.6) * mm});
            skLineSegment(sketch, "E245", {"start": v(27694.73, -91199.96) * mm, "end": v(27444.65, -92237.04) * mm});
            skLineSegment(sketch, "E246", {"start": v(27444.65, -92237.04) * mm, "end": v(27987.88, -92368.03) * mm});
            skLineSegment(sketch, "E247", {"start": v(27987.88, -92368.03) * mm, "end": v(28237.96, -91330.96) * mm});
            skLineSegment(sketch, "E248", {"start": v(27798.08, -88821.1) * mm, "end": v(27530.13, -89932.25) * mm});
            skLineSegment(sketch, "E249", {"start": v(27530.13, -89932.25) * mm, "end": v(25579.45, -89461.85) * mm});
            skLineSegment(sketch, "E250", {"start": v(25579.45, -89461.85) * mm, "end": v(25847.4, -88350.7) * mm});
            skLineSegment(sketch, "E251", {"start": v(27497.2, -91152.33) * mm, "end": v(27306.65, -91942.48) * mm});
            skLineSegment(sketch, "E252", {"start": v(27306.65, -91942.48) * mm, "end": v(26936.27, -91853.16) * mm});
            skLineSegment(sketch, "E253", {"start": v(26936.27, -91853.16) * mm, "end": v(27126.81, -91063.01) * mm});
            skLineSegment(sketch, "E254", {"start": v(24281.04, -90376.77) * mm, "end": v(26256.41, -90853.12) * mm});
            skLineSegment(sketch, "E255", {"start": v(26256.41, -90853.12) * mm, "end": v(25803.88, -92729.73) * mm});
            skLineSegment(sketch, "E256", {"start": v(27079.53, -90934.03) * mm, "end": v(27052.74, -91045.15) * mm});
            skLineSegment(sketch, "E257", {"start": v(26301.73, -90746.47) * mm, "end": v(26412.84, -90773.26) * mm});
            skLineSegment(sketch, "E258", {"start": v(13369.06, -90933.02) * mm, "end": v(13665.37, -91004.47) * mm});
            skLineSegment(sketch, "E259", {"start": v(14012.14, -88266.26) * mm, "end": v(14308.45, -88337.71) * mm});
            skLineSegment(sketch, "E260", {"start": v(14160.3, -88301.99) * mm, "end": v(13517.22, -90968.74) * mm});
            skLineSegment(sketch, "E261", {"start": v(30171.65, -79438.68) * mm, "end": v(31071.07, -80909.72) * mm});
            skLineSegment(sketch, "E262", {"start": v(30928.16, -81502.33) * mm, "end": v(30236.78, -81335.6) * mm});
            skLineSegment(sketch, "E263", {"start": v(30236.78, -81335.6) * mm, "end": v(29879.52, -82817.14) * mm});
            skLineSegment(sketch, "E264", {"start": v(29879.52, -82817.14) * mm, "end": v(30570.9, -82983.86) * mm});
            skLineSegment(sketch, "E265", {"start": v(25090.54, -81819.07) * mm, "end": v(25201.65, -81845.86) * mm});
            skLineSegment(sketch, "E266", {"start": v(24998.85, -83011.91) * mm, "end": v(25025.65, -82900.8) * mm});
            skLineSegment(sketch, "E267", {"start": v(25887.77, -83226.27) * mm, "end": v(25914.57, -83115.16) * mm});
            skLineSegment(sketch, "E268", {"start": v(25012.25, -82956.35) * mm, "end": v(25901.17, -83170.71) * mm});
            skArc(sketch, "E269", {"start": v(25901.17, -83170.71) * mm, "mid": v(25771.81, -82447.25) * mm, "end": v(25151.79, -82052.66) * mm, "construction": true});
            skLineSegment(sketch, "E270", {"start": v(28653.3, -83893.16) * mm, "end": v(28680.1, -83782.05) * mm});
            skLineSegment(sketch, "E271", {"start": v(29420.86, -83960.68) * mm, "end": v(29394.06, -84071.8) * mm});
            skLineSegment(sketch, "E272", {"start": v(30161.62, -84139.31) * mm, "end": v(30134.83, -84250.43) * mm});
            skLineSegment(sketch, "E273", {"start": v(28666.7, -83837.6) * mm, "end": v(29407.46, -84016.24) * mm});
            skLineSegment(sketch, "E274", {"start": v(29407.46, -84016.24) * mm, "end": v(30148.23, -84194.87) * mm});
            skLineSegment(sketch, "E275", {"start": v(26761.5, -78302.8) * mm, "end": v(26690.05, -78599.1) * mm});
            skLineSegment(sketch, "E276", {"start": v(27502.27, -78481.43) * mm, "end": v(27430.82, -78777.74) * mm});
            skLineSegment(sketch, "E277", {"start": v(27798.58, -78552.88) * mm, "end": v(27727.13, -78849.2) * mm});
            skLineSegment(sketch, "E278", {"start": v(28539.35, -78731.52) * mm, "end": v(28467.9, -79027.82) * mm});
            skLineSegment(sketch, "E279", {"start": v(28835.65, -78802.97) * mm, "end": v(28764.2, -79099.28) * mm});
            skLineSegment(sketch, "E280", {"start": v(29576.42, -78981.6) * mm, "end": v(29504.96, -79277.9) * mm});
            skLineSegment(sketch, "E281", {"start": v(27466.55, -78629.58) * mm, "end": v(26725.78, -78450.95) * mm});
            skLineSegment(sketch, "E282", {"start": v(27762.85, -78701.04) * mm, "end": v(28503.62, -78879.67) * mm});
            skLineSegment(sketch, "E283", {"start": v(28799.93, -78951.12) * mm, "end": v(29540.7, -79129.76) * mm});
            skLineSegment(sketch, "E284", {"start": v(26511.22, -82266.17) * mm, "end": v(26296.86, -83155.09) * mm});
            skLineSegment(sketch, "E285", {"start": v(26296.86, -83155.09) * mm, "end": v(28222.85, -83619.53) * mm});
            skLineSegment(sketch, "E286", {"start": v(28222.85, -83619.53) * mm, "end": v(28437.2, -82730.61) * mm});
            skLineSegment(sketch, "E287", {"start": v(28437.2, -82730.61) * mm, "end": v(26511.22, -82266.17) * mm});
            skLineSegment(sketch, "E288", {"start": v(27492.99, -78844.99) * mm, "end": v(29418.98, -79309.43) * mm});
            skLineSegment(sketch, "E289", {"start": v(29418.98, -79309.43) * mm, "end": v(29204.62, -80198.35) * mm});
            skLineSegment(sketch, "E290", {"start": v(29204.62, -80198.35) * mm, "end": v(27278.63, -79733.9) * mm});
            skLineSegment(sketch, "E291", {"start": v(27278.63, -79733.9) * mm, "end": v(27492.99, -78844.99) * mm});
            skLineSegment(sketch, "E292", {"start": v(14126.1, -76091.92) * mm, "end": v(14373.02, -76151.47) * mm});
            skLineSegment(sketch, "E293", {"start": v(14373.02, -76151.47) * mm, "end": v(13610.85, -79312.07) * mm});
            skLineSegment(sketch, "E294", {"start": v(13610.85, -79312.07) * mm, "end": v(13363.93, -79252.53) * mm});
            skLineSegment(sketch, "E295", {"start": v(13991.93, -77731.77) * mm, "end": v(13745.01, -77672.23) * mm});
            skLineSegment(sketch, "E296", {"start": v(13801.4, -78521.92) * mm, "end": v(13554.47, -78462.38) * mm});
            skLineSegment(sketch, "E297", {"start": v(14182.48, -76941.62) * mm, "end": v(13935.55, -76882.07) * mm});
            skLineSegment(sketch, "E298", {"start": v(14985.95, -75776.71) * mm, "end": v(14825.18, -76443.4) * mm});
            skLineSegment(sketch, "E299", {"start": v(14825.18, -76443.4) * mm, "end": v(18380.86, -77300.84) * mm});
            skLineSegment(sketch, "E300", {"start": v(17195.63, -77015.03) * mm, "end": v(17356.4, -76348.34) * mm});
            skLineSegment(sketch, "E301", {"start": v(16010.4, -76729.21) * mm, "end": v(16171.17, -76062.52) * mm});
            skLineSegment(sketch, "E302", {"start": v(18380.86, -77300.84) * mm, "end": v(18541.63, -76634.15) * mm});
            skLineSegment(sketch, "E303", {"start": v(14133.76, -79960.73) * mm, "end": v(14294.53, -79294.04) * mm});
            skLineSegment(sketch, "E304", {"start": v(14294.53, -79294.04) * mm, "end": v(17850.2, -80151.48) * mm});
            skLineSegment(sketch, "E305", {"start": v(17850.2, -80151.48) * mm, "end": v(17689.44, -80818.17) * mm});
            skLineSegment(sketch, "E306", {"start": v(15479.76, -79579.85) * mm, "end": v(15318.99, -80246.54) * mm});
            skLineSegment(sketch, "E307", {"start": v(16664.98, -79865.66) * mm, "end": v(16504.21, -80532.35) * mm});
            skLineSegment(sketch, "E308", {"start": v(18750.43, -79506.33) * mm, "end": v(19343.04, -79649.24) * mm});
            skLineSegment(sketch, "E309", {"start": v(18750.43, -79506.33) * mm, "end": v(18393.17, -80987.87) * mm});
            skLineSegment(sketch, "E310", {"start": v(19892.16, -77534.64) * mm, "end": v(20023.16, -76991.41) * mm});
            skLineSegment(sketch, "E311", {"start": v(18837.93, -76705.6) * mm, "end": v(18706.94, -77248.83) * mm});
            skLineSegment(sketch, "E312", {"start": v(18706.94, -77248.83) * mm, "end": v(19892.16, -77534.64) * mm});
            skLineSegment(sketch, "E313", {"start": v(18750.43, -79506.33) * mm, "end": v(18639.32, -79479.54) * mm});
            skLineSegment(sketch, "E314", {"start": v(18639.32, -79479.54) * mm, "end": v(18282.05, -80961.07) * mm});
            skLineSegment(sketch, "E315", {"start": v(25912.25, -78411.54) * mm, "end": v(26023.36, -78438.34) * mm});
            skLineSegment(sketch, "E316", {"start": v(15184.2, -82918.3) * mm, "end": v(15295.32, -82945.1) * mm});
            skLineSegment(sketch, "E317", {"start": v(14969.84, -83807.21) * mm, "end": v(15080.96, -83834) * mm});
            skLineSegment(sketch, "E318", {"start": v(7414.1, -79398.5) * mm, "end": v(7710.4, -79469.95) * mm});
            skLineSegment(sketch, "E319", {"start": v(6270.85, -84139.4) * mm, "end": v(6567.16, -84210.86) * mm});
            skLineSegment(sketch, "E320", {"start": v(19490.27, -92853.3) * mm, "end": v(19601.39, -92880.1) * mm});
            skLineSegment(sketch, "E321", {"start": v(19704.63, -91964.38) * mm, "end": v(19815.75, -91991.17) * mm});
            skSolve(sketch);
        }
        {
            var Q0;
            {var subQ6=sQuery(id+"F8.wireOp",EDGE,"E63");Q0=makeQuery(id+"F8.imprint","IMPRINT",FACE,{"disambiguationData":[TD([[makeQuery(id+"F8.imprint","IMPRINT",EDGE,{"derivedFrom":subQ6}),1.0]])]});}
            var Q1;
            {var subQ6=sQuery(id+"F8.wireOp",EDGE,"E62");Q1=makeQuery(id+"F8.imprint","IMPRINT",FACE,{"disambiguationData":[TD([[makeQuery(id+"F8.imprint","IMPRINT",EDGE,{"derivedFrom":subQ6}),1.0]])]});}
            var Q2;
            {var subQ14=sQuery(id+"F8.wireOp",EDGE,"E51");Q2=makeQuery(id+"F8.imprint","IMPRINT",FACE,{"disambiguationData":[TD([[makeQuery(id+"F8.imprint","IMPRINT",EDGE,{"derivedFrom":subQ14}),-1.0]])]});}
            var Q3;
            {var subQ0=sQuery(id+"F8.wireOp",EDGE,"E114");var subQ3=sQuery(id+"F8.wireOp",EDGE,"E55.11");var subQ4=makeQuery(id+"F8.imprint","INTERSECT",VERTEX,{"derivedFrom":[subQ3,subQ0]});Q3=makeQuery(id+"F8.imprint","IMPRINT",FACE,{"disambiguationData":[TD([[makeQuery(id+"F8.imprint","IMPRINT",EDGE,{"disambiguationData":[TD([[subQ4,-1.0]])],"derivedFrom":subQ3}),-1.0]])]});}
            var Q4;
            {var subQ4=sQuery(id+"F8.wireOp",EDGE,"E114");var subQ6=sQuery(id+"F8.wireOp",EDGE,"E216");var subQ7=makeQuery(id+"F8.imprint","INTERSECT",VERTEX,{"derivedFrom":[subQ4,subQ6]});Q4=makeQuery(id+"F8.imprint","IMPRINT",FACE,{"disambiguationData":[TD([[makeQuery(id+"F8.imprint","IMPRINT",EDGE,{"disambiguationData":[TD([[subQ7,-1.0]])],"derivedFrom":subQ4}),1.0]])]});}
            var Q5;
            {var subQ0=sQuery(id+"F8.wireOp",EDGE,"E217");Q5=makeQuery(id+"F8.imprint","IMPRINT",FACE,{"disambiguationData":[TD([[makeQuery(id+"F8.imprint","IMPRINT",EDGE,{"derivedFrom":subQ0}),1.0]])]});}
            var Q6;
            {var subQ16=sQuery(id+"F8.wireOp",EDGE,"E112");Q6=makeQuery(id+"F8.imprint","IMPRINT",FACE,{"disambiguationData":[TD([[makeQuery(id+"F8.imprint","IMPRINT",EDGE,{"derivedFrom":subQ16}),1.0]])]});}
            var Q7;
            {var subQ4=sQuery(id+"F8.wireOp",EDGE,"E120");var subQ6=makeQuery(id+"F8.imprint","INTERSECT",VERTEX,{"derivedFrom":[subQ4,sQuery(id+"F8.wireOp",EDGE,"E142")]});Q7=makeQuery(id+"F8.imprint","IMPRINT",FACE,{"disambiguationData":[TD([[makeQuery(id+"F8.imprint","IMPRINT",EDGE,{"disambiguationData":[TD([[subQ6,1.0]])],"derivedFrom":subQ4}),1.0]])]});}
            var Q8;
            {var subQ4=sQuery(id+"F8.wireOp",EDGE,"E122");var subQ6=makeQuery(id+"F8.imprint","INTERSECT",VERTEX,{"derivedFrom":[subQ4,sQuery(id+"F8.wireOp",EDGE,"E133")]});Q8=makeQuery(id+"F8.imprint","IMPRINT",FACE,{"disambiguationData":[TD([[makeQuery(id+"F8.imprint","IMPRINT",EDGE,{"disambiguationData":[TD([[subQ6,1.0]])],"derivedFrom":subQ4}),-1.0]])]});}
            var Q9;
            {var subQ1=sQuery(id+"F8.wireOp",EDGE,"E67");var subQ6=sQuery(id+"F8.wireOp",EDGE,"E122");var subQ7=makeQuery(id+"F8.imprint","INTERSECT",VERTEX,{"derivedFrom":[subQ1,subQ6]});Q9=makeQuery(id+"F8.imprint","IMPRINT",FACE,{"disambiguationData":[TD([[makeQuery(id+"F8.imprint","IMPRINT",EDGE,{"disambiguationData":[TD([[subQ7,1.0]])],"derivedFrom":subQ1}),-1.0]])]});}
            var Q10;
            {var subQ4=sQuery(id+"F8.wireOp",EDGE,"E121");var subQ5=sQuery(id+"F8.wireOp",EDGE,"E67");var subQ6=makeQuery(id+"F8.imprint","INTERSECT",VERTEX,{"derivedFrom":[subQ5,subQ4]});Q10=makeQuery(id+"F8.imprint","IMPRINT",FACE,{"disambiguationData":[TD([[makeQuery(id+"F8.imprint","IMPRINT",EDGE,{"disambiguationData":[TD([[subQ6,-1.0]])],"derivedFrom":subQ4}),-1.0]])]});}
            var Q11;
            {var subQ50=sQuery(id+"F8.wireOp",EDGE,"E27");Q11=makeQuery(id+"F8.imprint","IMPRINT",FACE,{"disambiguationData":[TD([[makeQuery(id+"F8.imprint","IMPRINT",EDGE,{"derivedFrom":subQ50}),1.0]])]});}
            var Q12;
            {var subQ4=sQuery(id+"F8.wireOp",EDGE,"E208");Q12=makeQuery(id+"F8.imprint","IMPRINT",FACE,{"disambiguationData":[TD([[makeQuery(id+"F8.imprint","IMPRINT",EDGE,{"derivedFrom":subQ4}),-1.0]])]});}
            var Q13;
            {var subQ4=sQuery(id+"F8.wireOp",EDGE,"E201");Q13=makeQuery(id+"F8.imprint","IMPRINT",FACE,{"disambiguationData":[TD([[makeQuery(id+"F8.imprint","IMPRINT",EDGE,{"derivedFrom":subQ4}),1.0]])]});}
            var Q14;
            {var subQ1=sQuery(id+"F8.wireOp",EDGE,"E200");var subQ5=sQuery(id+"F8.wireOp",EDGE,"E173");var subQ8=makeQuery(id+"F8.imprint","INTERSECT",VERTEX,{"derivedFrom":[subQ5,subQ1]});Q14=makeQuery(id+"F8.imprint","IMPRINT",FACE,{"disambiguationData":[TD([[makeQuery(id+"F8.imprint","IMPRINT",EDGE,{"disambiguationData":[TD([[subQ8,-1.0]])],"derivedFrom":subQ5}),-1.0]])]});}
            var Q15;
            {var subQ1=sQuery(id+"F8.wireOp",EDGE,"E172");var subQ12=makeQuery(id+"F8.imprint","INTERSECT",VERTEX,{"derivedFrom":[subQ1,sQuery(id+"F8.wireOp",EDGE,"E176")]});Q15=makeQuery(id+"F8.imprint","IMPRINT",FACE,{"disambiguationData":[TD([[makeQuery(id+"F8.imprint","IMPRINT",EDGE,{"disambiguationData":[TD([[subQ12,1.0]])],"derivedFrom":subQ1}),-1.0]])]});}
            var Q16;
            {var subQ4=sQuery(id+"F8.wireOp",EDGE,"E171");var subQ6=sQuery(id+"F8.wireOp",EDGE,"E172");var subQ7=makeQuery(id+"F8.imprint","INTERSECT",VERTEX,{"derivedFrom":[subQ4,subQ6]});Q16=makeQuery(id+"F8.imprint","IMPRINT",FACE,{"disambiguationData":[TD([[makeQuery(id+"F8.imprint","IMPRINT",EDGE,{"disambiguationData":[TD([[subQ7,-1.0]])],"derivedFrom":subQ4}),1.0]])]});}
            var Q17;
            {var subQ5=sQuery(id+"F8.wireOp",EDGE,"E91");Q17=makeQuery(id+"F8.imprint","IMPRINT",FACE,{"disambiguationData":[TD([[makeQuery(id+"F8.imprint","IMPRINT",EDGE,{"derivedFrom":subQ5}),1.0]])]});}
            var Q18;
            {var subQ7=sQuery(id+"F8.wireOp",EDGE,"E175");Q18=makeQuery(id+"F8.imprint","IMPRINT",FACE,{"disambiguationData":[TD([[makeQuery(id+"F8.imprint","IMPRINT",EDGE,{"derivedFrom":subQ7}),1.0]])]});}
            var Q19;
            {var subQ0=sQuery(id+"F8.wireOp",EDGE,"E189");Q19=makeQuery(id+"F8.imprint","IMPRINT",FACE,{"disambiguationData":[TD([[makeQuery(id+"F8.imprint","IMPRINT",EDGE,{"derivedFrom":subQ0}),1.0]])]});}
            var Q20;
            {var subQ1=sQuery(id+"F8.wireOp",EDGE,"E172");var subQ4=sQuery(id+"F8.wireOp",EDGE,"E78.trimOffspring");var subQ5=makeQuery(id+"F8.imprint","INTERSECT",VERTEX,{"derivedFrom":[subQ4,subQ1]});Q20=makeQuery(id+"F8.imprint","IMPRINT",FACE,{"disambiguationData":[TD([[makeQuery(id+"F8.imprint","IMPRINT",EDGE,{"disambiguationData":[TD([[subQ5,1.0]])],"derivedFrom":subQ4}),1.0]])]});}
            var Q21;
            {var subQ1=sQuery(id+"F8.wireOp",EDGE,"E82");var subQ4=sQuery(id+"F8.wireOp",EDGE,"E78.trimOffspring");var subQ5=makeQuery(id+"F8.imprint","INTERSECT",VERTEX,{"derivedFrom":[subQ4,subQ1]});Q21=makeQuery(id+"F8.imprint","IMPRINT",FACE,{"disambiguationData":[TD([[makeQuery(id+"F8.imprint","IMPRINT",EDGE,{"disambiguationData":[TD([[subQ5,1.0]])],"derivedFrom":subQ4}),1.0]])]});}
            var Q22;
            {var subQ4=sQuery(id+"F8.wireOp",EDGE,"E267");var subQ5=sQuery(id+"F8.wireOp",EDGE,"E82");var subQ6=makeQuery(id+"F8.imprint","INTERSECT",VERTEX,{"derivedFrom":[subQ5,subQ4]});Q22=makeQuery(id+"F8.imprint","IMPRINT",FACE,{"disambiguationData":[TD([[makeQuery(id+"F8.imprint","IMPRINT",EDGE,{"disambiguationData":[TD([[subQ6,-1.0]])],"derivedFrom":subQ5}),-1.0]])]});}
            var Q23;
            {var subQ11=sQuery(id+"F8.wireOp",EDGE,"E81");Q23=makeQuery(id+"F8.imprint","IMPRINT",FACE,{"disambiguationData":[TD([[makeQuery(id+"F8.imprint","IMPRINT",EDGE,{"derivedFrom":subQ11}),-1.0]])]});}
            var Q24;
            {var subQ0=sQuery(id+"F8.wireOp",EDGE,"E276");var subQ4=sQuery(id+"F8.wireOp",EDGE,"E53");var subQ5=makeQuery(id+"F8.imprint","INTERSECT",VERTEX,{"derivedFrom":[subQ4,subQ0]});Q24=makeQuery(id+"F8.imprint","IMPRINT",FACE,{"disambiguationData":[TD([[makeQuery(id+"F8.imprint","IMPRINT",EDGE,{"disambiguationData":[TD([[subQ5,-1.0]])],"derivedFrom":subQ4}),-1.0]])]});}
            var Q25;
            {var subQ0=sQuery(id+"F8.wireOp",EDGE,"E278");var subQ4=sQuery(id+"F8.wireOp",EDGE,"E53");var subQ5=makeQuery(id+"F8.imprint","INTERSECT",VERTEX,{"derivedFrom":[subQ4,subQ0]});Q25=makeQuery(id+"F8.imprint","IMPRINT",FACE,{"disambiguationData":[TD([[makeQuery(id+"F8.imprint","IMPRINT",EDGE,{"disambiguationData":[TD([[subQ5,-1.0]])],"derivedFrom":subQ4}),-1.0]])]});}
            var Q26;
            {var subQ9=sQuery(id+"F8.wireOp",EDGE,"E59");var subQ11=makeQuery(id+"F8.imprint","INTERSECT",VERTEX,{"derivedFrom":[subQ9,sQuery(id+"F8.wireOp",EDGE,"E161")]});Q26=makeQuery(id+"F8.imprint","IMPRINT",FACE,{"disambiguationData":[TD([[makeQuery(id+"F8.imprint","IMPRINT",EDGE,{"disambiguationData":[TD([[subQ11,1.0]])],"derivedFrom":subQ9}),-1.0]])]});}
            var Q27;
            {var subQ4=sQuery(id+"F8.wireOp",EDGE,"E114");var subQ5=sQuery(id+"F8.wireOp",EDGE,"E61");var subQ6=makeQuery(id+"F8.imprint","INTERSECT",VERTEX,{"derivedFrom":[subQ5,subQ4]});Q27=makeQuery(id+"F8.imprint","IMPRINT",FACE,{"disambiguationData":[TD([[makeQuery(id+"F8.imprint","IMPRINT",EDGE,{"disambiguationData":[TD([[subQ6,1.0]])],"derivedFrom":subQ5}),-1.0]])]});}
            var Q28;
            {var subQ0=sQuery(id+"F8.wireOp",EDGE,"E115");Q28=makeQuery(id+"F8.imprint","IMPRINT",FACE,{"disambiguationData":[TD([[makeQuery(id+"F8.imprint","IMPRINT",EDGE,{"derivedFrom":subQ0}),-1.0]])]});}
            var Q29;
            {var subQ0=sQuery(id+"F8.wireOp",EDGE,"E309");Q29=makeQuery(id+"F8.imprint","IMPRINT",FACE,{"disambiguationData":[TD([[makeQuery(id+"F8.imprint","IMPRINT",EDGE,{"derivedFrom":subQ0}),-1.0]])]});}
            var Q30;
            {var subQ5=sQuery(id+"F8.wireOp",EDGE,"E117");var subQ10=sQuery(id+"F8.wireOp",EDGE,"E50");var subQ11=makeQuery(id+"F8.imprint","INTERSECT",VERTEX,{"derivedFrom":[subQ10,subQ5]});Q30=makeQuery(id+"F8.imprint","IMPRINT",FACE,{"disambiguationData":[TD([[makeQuery(id+"F8.imprint","IMPRINT",EDGE,{"disambiguationData":[TD([[subQ11,-1.0]])],"derivedFrom":subQ10}),-1.0]])]});}
            var Q31;
            {var subQ4=sQuery(id+"F8.wireOp",EDGE,"E55.9");var subQ7=makeQuery(id+"F8.imprint","INTERSECT",VERTEX,{"derivedFrom":[subQ4,sQuery(id+"F8.wireOp",EDGE,"E68")]});Q31=makeQuery(id+"F8.imprint","IMPRINT",FACE,{"disambiguationData":[TD([[makeQuery(id+"F8.imprint","IMPRINT",EDGE,{"disambiguationData":[TD([[subQ7,1.0]])],"derivedFrom":subQ4}),-1.0]])]});}
            var Q32;
            {var subQ0=sQuery(id+"F8.wireOp",EDGE,"E240");Q32=makeQuery(id+"F8.imprint","IMPRINT",FACE,{"disambiguationData":[TD([[makeQuery(id+"F8.imprint","IMPRINT",EDGE,{"derivedFrom":subQ0}),-1.0]])]});}
            var Q33;
            {var subQ6=sQuery(id+"F8.wireOp",EDGE,"E242");Q33=makeQuery(id+"F8.imprint","IMPRINT",FACE,{"disambiguationData":[TD([[makeQuery(id+"F8.imprint","IMPRINT",EDGE,{"derivedFrom":subQ6}),-1.0]])]});}
            var Q34;
            {var subQ3=sQuery(id+"F8.wireOp",EDGE,"E261");Q34=makeQuery(id+"F8.imprint","IMPRINT",FACE,{"disambiguationData":[TD([[makeQuery(id+"F8.imprint","IMPRINT",EDGE,{"derivedFrom":subQ3}),1.0]])]});}
            var Q35;
            {var subQ2=sQuery(id+"F8.wireOp",EDGE,"E316");Q35=makeQuery(id+"F8.imprint","IMPRINT",FACE,{"disambiguationData":[TD([[makeQuery(id+"F8.imprint","IMPRINT",EDGE,{"derivedFrom":subQ2}),1.0]])]});}
            var Q36;
            {var subQ4=sQuery(id+"F8.wireOp",EDGE,"E58.1");Q36=makeQuery(id+"F8.imprint","IMPRINT",FACE,{"disambiguationData":[TD([[makeQuery(id+"F8.imprint","IMPRINT",EDGE,{"derivedFrom":subQ4}),1.0]])]});}
            var Q37;
            {var subQ5=sQuery(id+"F8.wireOp",EDGE,"E320");Q37=makeQuery(id+"F8.imprint","IMPRINT",FACE,{"disambiguationData":[TD([[makeQuery(id+"F8.imprint","IMPRINT",EDGE,{"derivedFrom":subQ5}),-1.0]])]});}
            extrude(context, id + "F9", {"entities" : qUnion([Q0, Q1, Q2, Q3, Q4, Q5, Q6, Q7, Q8, Q9, Q10, Q11, Q12, Q13, Q14, Q15, Q16, Q17, Q18, Q19, Q20, Q21, Q22, Q23, Q24, Q25, Q26, Q27, Q28, Q29, Q30, Q31, Q32, Q33, Q34, Q35, Q36, Q37]), "operationType" : NewBodyOperationType.ADD, "depth" : 2743.2 * mm, "offsetDistance" : 25.4 * mm});
        }
        {
            var Q0;
            Q0=makeQuery(id+"F8.imprint","IMPRINT",FACE,{"disambiguationData":[TD([[makeQuery(id+"F8.imprint","IMPRINT",EDGE,{"derivedFrom":sQuery(id+"F8.wireOp",EDGE,"E97")}),1.0]])]});
            var Q1;
            Q1=makeQuery(id+"F8.imprint","IMPRINT",FACE,{"disambiguationData":[TD([[makeQuery(id+"F8.imprint","IMPRINT",EDGE,{"derivedFrom":sQuery(id+"F8.wireOp",EDGE,"E98")}),1.0]])]});
            var Q2;
            {var subQ3=sQuery(id+"F8.wireOp",EDGE,"E96");Q2=makeQuery(id+"F8.imprint","IMPRINT",FACE,{"disambiguationData":[TD([[makeQuery(id+"F8.imprint","IMPRINT",EDGE,{"derivedFrom":subQ3}),1.0]])]});}
            var Q3;
            {var subQ3=sQuery(id+"F8.wireOp",EDGE,"E94");Q3=makeQuery(id+"F8.imprint","IMPRINT",FACE,{"disambiguationData":[TD([[makeQuery(id+"F8.imprint","IMPRINT",EDGE,{"derivedFrom":subQ3}),1.0]])]});}
            extrude(context, id + "F10", {"entities" : qUnion([Q0, Q1, Q2, Q3]), "operationType" : NewBodyOperationType.ADD, "depth" : 914.4 * mm, "offsetDistance" : 25.4 * mm});
        }
        {
            var Q0;
            {var subQ0=sQuery(id+"F8.wireOp",EDGE,"E310");Q0=makeQuery(id+"F8.imprint","IMPRINT",FACE,{"disambiguationData":[TD([[makeQuery(id+"F8.imprint","IMPRINT",EDGE,{"derivedFrom":subQ0}),1.0]])]});}
            extrude(context, id + "F11", {"entities" : qUnion([Q0]), "operationType" : NewBodyOperationType.ADD, "depth" : 2133.6 * mm, "offsetDistance" : 25.4 * mm});
        }
        {
            var Q0;
            {var subQ0=sQuery(id+"F8.wireOp",EDGE,"E298");Q0=makeQuery(id+"F8.imprint","IMPRINT",FACE,{"disambiguationData":[TD([[makeQuery(id+"F8.imprint","IMPRINT",EDGE,{"derivedFrom":subQ0}),1.0]])]});}
            var Q1;
            {var subQ0=sQuery(id+"F8.wireOp",EDGE,"E300");Q1=makeQuery(id+"F8.imprint","IMPRINT",FACE,{"disambiguationData":[TD([[makeQuery(id+"F8.imprint","IMPRINT",EDGE,{"derivedFrom":subQ0}),1.0]])]});}
            var Q2;
            {var subQ0=sQuery(id+"F8.wireOp",EDGE,"E300");Q2=makeQuery(id+"F8.imprint","IMPRINT",FACE,{"disambiguationData":[TD([[makeQuery(id+"F8.imprint","IMPRINT",EDGE,{"derivedFrom":subQ0}),-1.0]])]});}
            var Q3;
            {var subQ0=sQuery(id+"F8.wireOp",EDGE,"E303");Q3=makeQuery(id+"F8.imprint","IMPRINT",FACE,{"disambiguationData":[TD([[makeQuery(id+"F8.imprint","IMPRINT",EDGE,{"derivedFrom":subQ0}),-1.0]])]});}
            var Q4;
            {var subQ0=sQuery(id+"F8.wireOp",EDGE,"E306");Q4=makeQuery(id+"F8.imprint","IMPRINT",FACE,{"disambiguationData":[TD([[makeQuery(id+"F8.imprint","IMPRINT",EDGE,{"derivedFrom":subQ0}),1.0]])]});}
            var Q5;
            {var subQ0=sQuery(id+"F8.wireOp",EDGE,"E305");Q5=makeQuery(id+"F8.imprint","IMPRINT",FACE,{"disambiguationData":[TD([[makeQuery(id+"F8.imprint","IMPRINT",EDGE,{"derivedFrom":subQ0}),-1.0]])]});}
            extrude(context, id + "F12", {"entities" : qUnion([Q0, Q1, Q2, Q3, Q4, Q5]), "operationType" : NewBodyOperationType.ADD, "depth" : 762 * mm, "offsetDistance" : 25.4 * mm, "hasSecondDirection" : true, "secondDirectionOppositeDirection" : true, "secondDirectionDepth" : -711.2 * mm});
        }
        {
            var Q0;
            {var subQ0=sQuery(id+"F8.wireOp",EDGE,"E294");Q0=makeQuery(id+"F8.imprint","IMPRINT",FACE,{"disambiguationData":[TD([[makeQuery(id+"F8.imprint","IMPRINT",EDGE,{"derivedFrom":subQ0}),-1.0]])]});}
            var Q1;
            {var subQ0=sQuery(id+"F8.wireOp",EDGE,"E292");Q1=makeQuery(id+"F8.imprint","IMPRINT",FACE,{"disambiguationData":[TD([[makeQuery(id+"F8.imprint","IMPRINT",EDGE,{"derivedFrom":subQ0}),-1.0]])]});}
            extrude(context, id + "F13", {"entities" : qUnion([Q0, Q1]), "operationType" : NewBodyOperationType.ADD, "depth" : 1981.2 * mm, "offsetDistance" : 25.4 * mm});
        }
        {
            var Q0;
            {var subQ0=sQuery(id+"F8.wireOp",EDGE,"E295");Q0=makeQuery(id+"F8.imprint","IMPRINT",FACE,{"disambiguationData":[TD([[makeQuery(id+"F8.imprint","IMPRINT",EDGE,{"derivedFrom":subQ0}),1.0]])]});}
            var Q1;
            {var subQ0=sQuery(id+"F8.wireOp",EDGE,"E295");Q1=makeQuery(id+"F8.imprint","IMPRINT",FACE,{"disambiguationData":[TD([[makeQuery(id+"F8.imprint","IMPRINT",EDGE,{"derivedFrom":subQ0}),-1.0]])]});}
            extrude(context, id + "F14", {"entities" : qUnion([Q0, Q1]), "operationType" : NewBodyOperationType.ADD, "depth" : 2133.6 * mm, "offsetDistance" : 25.4 * mm});
        }
        {
            var Q0;
            Q0=makeQuery(id+"F8.imprint","IMPRINT",FACE,{"disambiguationData":[TD([[makeQuery(id+"F8.imprint","IMPRINT",EDGE,{"derivedFrom":sQuery(id+"F8.wireOp",EDGE,"E85")}),-1.0]])]});
            extrude(context, id + "F15", {"entities" : qUnion([Q0]), "operationType" : NewBodyOperationType.ADD, "depth" : 787.4 * mm, "offsetDistance" : 25.4 * mm});
        }
        {
            var Q0;
            {var subQ0=sQuery(id+"F8.wireOp",EDGE,"E262");Q0=makeQuery(id+"F8.imprint","IMPRINT",FACE,{"disambiguationData":[TD([[makeQuery(id+"F8.imprint","IMPRINT",EDGE,{"derivedFrom":subQ0}),1.0]])]});}
            extrude(context, id + "F16", {"entities" : qUnion([Q0]), "operationType" : NewBodyOperationType.ADD, "depth" : 2590.8 * mm, "offsetDistance" : 25.4 * mm});
        }
        {
            var Q0;
            {var subQ5=sQuery(id+"F8.wireOp",EDGE,"E281");Q0=makeQuery(id+"F8.imprint","IMPRINT",FACE,{"disambiguationData":[TD([[makeQuery(id+"F8.imprint","IMPRINT",EDGE,{"derivedFrom":subQ5}),-1.0]])]});}
            var Q1;
            {var subQ5=sQuery(id+"F8.wireOp",EDGE,"E281");Q1=makeQuery(id+"F8.imprint","IMPRINT",FACE,{"disambiguationData":[TD([[makeQuery(id+"F8.imprint","IMPRINT",EDGE,{"derivedFrom":subQ5}),1.0]])]});}
            var Q2;
            {var subQ5=sQuery(id+"F8.wireOp",EDGE,"E282");Q2=makeQuery(id+"F8.imprint","IMPRINT",FACE,{"disambiguationData":[TD([[makeQuery(id+"F8.imprint","IMPRINT",EDGE,{"derivedFrom":subQ5}),1.0]])]});}
            var Q3;
            {var subQ5=sQuery(id+"F8.wireOp",EDGE,"E282");Q3=makeQuery(id+"F8.imprint","IMPRINT",FACE,{"disambiguationData":[TD([[makeQuery(id+"F8.imprint","IMPRINT",EDGE,{"derivedFrom":subQ5}),-1.0]])]});}
            var Q4;
            {var subQ5=sQuery(id+"F8.wireOp",EDGE,"E283");Q4=makeQuery(id+"F8.imprint","IMPRINT",FACE,{"disambiguationData":[TD([[makeQuery(id+"F8.imprint","IMPRINT",EDGE,{"derivedFrom":subQ5}),-1.0]])]});}
            var Q5;
            {var subQ5=sQuery(id+"F8.wireOp",EDGE,"E283");Q5=makeQuery(id+"F8.imprint","IMPRINT",FACE,{"disambiguationData":[TD([[makeQuery(id+"F8.imprint","IMPRINT",EDGE,{"derivedFrom":subQ5}),1.0]])]});}
            extrude(context, id + "F17", {"entities" : qUnion([Q0, Q1, Q2, Q3, Q4, Q5]), "operationType" : NewBodyOperationType.ADD, "depth" : 609.6 * mm, "offsetDistance" : 25.4 * mm});
        }
        {
            var Q0;
            {var subQ3=sQuery(id+"F8.wireOp",EDGE,"E133");Q0=makeQuery(id+"F8.imprint","IMPRINT",FACE,{"disambiguationData":[TD([[makeQuery(id+"F8.imprint","IMPRINT",EDGE,{"derivedFrom":subQ3}),1.0]])]});}
            var Q1;
            {var subQ3=sQuery(id+"F8.wireOp",EDGE,"E149");Q1=makeQuery(id+"F8.imprint","IMPRINT",FACE,{"disambiguationData":[TD([[makeQuery(id+"F8.imprint","IMPRINT",EDGE,{"derivedFrom":subQ3}),1.0]])]});}
            var Q2;
            {var subQ4=sQuery(id+"F8.wireOp",EDGE,"E156");Q2=makeQuery(id+"F8.imprint","IMPRINT",FACE,{"disambiguationData":[TD([[makeQuery(id+"F8.imprint","IMPRINT",EDGE,{"derivedFrom":subQ4}),-1.0]])]});}
            var Q3;
            {var subQ3=sQuery(id+"F8.wireOp",EDGE,"E142");Q3=makeQuery(id+"F8.imprint","IMPRINT",FACE,{"disambiguationData":[TD([[makeQuery(id+"F8.imprint","IMPRINT",EDGE,{"derivedFrom":subQ3}),1.0]])]});}
            extrude(context, id + "F18", {"entities" : qUnion([Q0, Q1, Q2, Q3]), "operationType" : NewBodyOperationType.ADD, "depth" : 2438.4 * mm, "offsetDistance" : 25.4 * mm});
        }
        {
            var Q0;
            {var subQ0=sQuery(id+"F8.wireOp",EDGE,"E130");Q0=makeQuery(id+"F8.imprint","IMPRINT",FACE,{"disambiguationData":[TD([[makeQuery(id+"F8.imprint","IMPRINT",EDGE,{"derivedFrom":subQ0}),-1.0]])]});}
            var Q1;
            {var subQ0=sQuery(id+"F8.wireOp",EDGE,"E182");Q1=makeQuery(id+"F8.imprint","IMPRINT",FACE,{"disambiguationData":[TD([[makeQuery(id+"F8.imprint","IMPRINT",EDGE,{"derivedFrom":subQ0}),1.0]])]});}
            extrude(context, id + "F19", {"entities" : qUnion([Q0, Q1]), "operationType" : NewBodyOperationType.ADD, "depth" : 381 * mm, "offsetDistance" : 25.4 * mm});
        }
        {
            var Q0;
            {var subQ3=sQuery(id+"F8.wireOp",EDGE,"E127");Q0=makeQuery(id+"F8.imprint","IMPRINT",FACE,{"disambiguationData":[TD([[makeQuery(id+"F8.imprint","IMPRINT",EDGE,{"derivedFrom":subQ3}),-1.0]])]});}
            var Q1;
            {var subQ1=sQuery(id+"F8.wireOp",EDGE,"E179");Q1=makeQuery(id+"F8.imprint","IMPRINT",FACE,{"disambiguationData":[TD([[makeQuery(id+"F8.imprint","IMPRINT",EDGE,{"derivedFrom":subQ1}),1.0]])]});}
            extrude(context, id + "F20", {"entities" : qUnion([Q0, Q1]), "operationType" : NewBodyOperationType.ADD, "depth" : 762 * mm, "offsetDistance" : 25.4 * mm});
        }
        {
            var Q0;
            {var subQ4=sQuery(id+"F8.wireOp",EDGE,"E177");Q0=makeQuery(id+"F8.imprint","IMPRINT",FACE,{"disambiguationData":[TD([[makeQuery(id+"F8.imprint","IMPRINT",EDGE,{"derivedFrom":subQ4}),1.0]])]});}
            var Q1;
            {var subQ0=sQuery(id+"F8.wireOp",EDGE,"E124");Q1=makeQuery(id+"F8.imprint","IMPRINT",FACE,{"disambiguationData":[TD([[makeQuery(id+"F8.imprint","IMPRINT",EDGE,{"derivedFrom":subQ0}),-1.0]])]});}
            extrude(context, id + "F21", {"entities" : qUnion([Q0, Q1]), "operationType" : NewBodyOperationType.ADD, "depth" : 787.4 * mm, "offsetDistance" : 25.4 * mm});
        }
        {
            var Q0;
            {var subQ0=sQuery(id+"F8.wireOp",EDGE,"E175");Q0=makeQuery(id+"F8.imprint","IMPRINT",FACE,{"disambiguationData":[TD([[makeQuery(id+"F8.imprint","IMPRINT",EDGE,{"derivedFrom":subQ0}),-1.0]])]});}
            extrude(context, id + "F22", {"entities" : qUnion([Q0]), "operationType" : NewBodyOperationType.ADD, "depth" : 508 * mm, "offsetDistance" : 25.4 * mm});
        }
        {
            var Q0;
            {var subQ0=sQuery(id+"F8.wireOp",EDGE,"E191");Q0=makeQuery(id+"F8.imprint","IMPRINT",FACE,{"disambiguationData":[TD([[makeQuery(id+"F8.imprint","IMPRINT",EDGE,{"derivedFrom":subQ0}),-1.0]])]});}
            extrude(context, id + "F23", {"entities" : qUnion([Q0]), "operationType" : NewBodyOperationType.ADD, "depth" : 508 * mm, "offsetDistance" : 25.4 * mm});
        }
        {
            var Q0;
            {var subQ5=sQuery(id+"F8.wireOp",EDGE,"E187");Q0=makeQuery(id+"F8.imprint","IMPRINT",FACE,{"disambiguationData":[TD([[makeQuery(id+"F8.imprint","IMPRINT",EDGE,{"derivedFrom":subQ5}),1.0]])]});}
            var Q1;
            {var subQ5=sQuery(id+"F8.wireOp",EDGE,"E187");Q1=makeQuery(id+"F8.imprint","IMPRINT",FACE,{"disambiguationData":[TD([[makeQuery(id+"F8.imprint","IMPRINT",EDGE,{"derivedFrom":subQ5}),-1.0]])]});}
            var Q2;
            {var subQ5=sQuery(id+"F8.wireOp",EDGE,"E206");Q2=makeQuery(id+"F8.imprint","IMPRINT",FACE,{"disambiguationData":[TD([[makeQuery(id+"F8.imprint","IMPRINT",EDGE,{"derivedFrom":subQ5}),1.0]])]});}
            var Q3;
            {var subQ5=sQuery(id+"F8.wireOp",EDGE,"E206");Q3=makeQuery(id+"F8.imprint","IMPRINT",FACE,{"disambiguationData":[TD([[makeQuery(id+"F8.imprint","IMPRINT",EDGE,{"derivedFrom":subQ5}),-1.0]])]});}
            var Q4;
            {var subQ5=sQuery(id+"F8.wireOp",EDGE,"E197");Q4=makeQuery(id+"F8.imprint","IMPRINT",FACE,{"disambiguationData":[TD([[makeQuery(id+"F8.imprint","IMPRINT",EDGE,{"derivedFrom":subQ5}),1.0]])]});}
            var Q5;
            {var subQ5=sQuery(id+"F8.wireOp",EDGE,"E197");Q5=makeQuery(id+"F8.imprint","IMPRINT",FACE,{"disambiguationData":[TD([[makeQuery(id+"F8.imprint","IMPRINT",EDGE,{"derivedFrom":subQ5}),-1.0]])]});}
            var Q6;
            {var subQ5=sQuery(id+"F8.wireOp",EDGE,"E198");Q6=makeQuery(id+"F8.imprint","IMPRINT",FACE,{"disambiguationData":[TD([[makeQuery(id+"F8.imprint","IMPRINT",EDGE,{"derivedFrom":subQ5}),1.0]])]});}
            var Q7;
            {var subQ5=sQuery(id+"F8.wireOp",EDGE,"E198");Q7=makeQuery(id+"F8.imprint","IMPRINT",FACE,{"disambiguationData":[TD([[makeQuery(id+"F8.imprint","IMPRINT",EDGE,{"derivedFrom":subQ5}),-1.0]])]});}
            var Q8;
            {var subQ5=sQuery(id+"F8.wireOp",EDGE,"E273");Q8=makeQuery(id+"F8.imprint","IMPRINT",FACE,{"disambiguationData":[TD([[makeQuery(id+"F8.imprint","IMPRINT",EDGE,{"derivedFrom":subQ5}),1.0]])]});}
            var Q9;
            {var subQ5=sQuery(id+"F8.wireOp",EDGE,"E273");Q9=makeQuery(id+"F8.imprint","IMPRINT",FACE,{"disambiguationData":[TD([[makeQuery(id+"F8.imprint","IMPRINT",EDGE,{"derivedFrom":subQ5}),-1.0]])]});}
            var Q10;
            {var subQ5=sQuery(id+"F8.wireOp",EDGE,"E274");Q10=makeQuery(id+"F8.imprint","IMPRINT",FACE,{"disambiguationData":[TD([[makeQuery(id+"F8.imprint","IMPRINT",EDGE,{"derivedFrom":subQ5}),1.0]])]});}
            var Q11;
            {var subQ5=sQuery(id+"F8.wireOp",EDGE,"E274");Q11=makeQuery(id+"F8.imprint","IMPRINT",FACE,{"disambiguationData":[TD([[makeQuery(id+"F8.imprint","IMPRINT",EDGE,{"derivedFrom":subQ5}),-1.0]])]});}
            var Q12;
            {var subQ5=sQuery(id+"F8.wireOp",EDGE,"E268");Q12=makeQuery(id+"F8.imprint","IMPRINT",FACE,{"disambiguationData":[TD([[makeQuery(id+"F8.imprint","IMPRINT",EDGE,{"derivedFrom":subQ5}),1.0]])]});}
            var Q13;
            {var subQ5=sQuery(id+"F8.wireOp",EDGE,"E268");Q13=makeQuery(id+"F8.imprint","IMPRINT",FACE,{"disambiguationData":[TD([[makeQuery(id+"F8.imprint","IMPRINT",EDGE,{"derivedFrom":subQ5}),-1.0]])]});}
            var Q14;
            {var subQ5=sQuery(id+"F8.wireOp",EDGE,"E106");Q14=makeQuery(id+"F8.imprint","IMPRINT",FACE,{"disambiguationData":[TD([[makeQuery(id+"F8.imprint","IMPRINT",EDGE,{"derivedFrom":subQ5}),1.0]])]});}
            var Q15;
            {var subQ0=sQuery(id+"F8.wireOp",EDGE,"E106");Q15=makeQuery(id+"F8.imprint","IMPRINT",FACE,{"disambiguationData":[TD([[makeQuery(id+"F8.imprint","IMPRINT",EDGE,{"derivedFrom":subQ0}),-1.0]])]});}
            var Q16;
            {var subQ5=sQuery(id+"F8.wireOp",EDGE,"E107");Q16=makeQuery(id+"F8.imprint","IMPRINT",FACE,{"disambiguationData":[TD([[makeQuery(id+"F8.imprint","IMPRINT",EDGE,{"derivedFrom":subQ5}),-1.0]])]});}
            var Q17;
            {var subQ5=sQuery(id+"F8.wireOp",EDGE,"E110");Q17=makeQuery(id+"F8.imprint","IMPRINT",FACE,{"disambiguationData":[TD([[makeQuery(id+"F8.imprint","IMPRINT",EDGE,{"derivedFrom":subQ5}),1.0]])]});}
            var Q18;
            {var subQ0=sQuery(id+"F8.wireOp",EDGE,"E110");Q18=makeQuery(id+"F8.imprint","IMPRINT",FACE,{"disambiguationData":[TD([[makeQuery(id+"F8.imprint","IMPRINT",EDGE,{"derivedFrom":subQ0}),-1.0]])]});}
            var Q19;
            {var subQ5=sQuery(id+"F8.wireOp",EDGE,"E111");Q19=makeQuery(id+"F8.imprint","IMPRINT",FACE,{"disambiguationData":[TD([[makeQuery(id+"F8.imprint","IMPRINT",EDGE,{"derivedFrom":subQ5}),-1.0]])]});}
            var Q20;
            {var subQ5=sQuery(id+"F8.wireOp",EDGE,"E154");Q20=makeQuery(id+"F8.imprint","IMPRINT",FACE,{"disambiguationData":[TD([[makeQuery(id+"F8.imprint","IMPRINT",EDGE,{"derivedFrom":subQ5}),1.0]])]});}
            var Q21;
            {var subQ3=sQuery(id+"F8.wireOp",EDGE,"E154");Q21=makeQuery(id+"F8.imprint","IMPRINT",FACE,{"disambiguationData":[TD([[makeQuery(id+"F8.imprint","IMPRINT",EDGE,{"derivedFrom":subQ3}),-1.0]])]});}
            var Q22;
            {var subQ5=sQuery(id+"F8.wireOp",EDGE,"E145");Q22=makeQuery(id+"F8.imprint","IMPRINT",FACE,{"disambiguationData":[TD([[makeQuery(id+"F8.imprint","IMPRINT",EDGE,{"derivedFrom":subQ5}),1.0]])]});}
            var Q23;
            {var subQ5=sQuery(id+"F8.wireOp",EDGE,"E145");Q23=makeQuery(id+"F8.imprint","IMPRINT",FACE,{"disambiguationData":[TD([[makeQuery(id+"F8.imprint","IMPRINT",EDGE,{"derivedFrom":subQ5}),-1.0]])]});}
            var Q24;
            {var subQ5=sQuery(id+"F8.wireOp",EDGE,"E136");Q24=makeQuery(id+"F8.imprint","IMPRINT",FACE,{"disambiguationData":[TD([[makeQuery(id+"F8.imprint","IMPRINT",EDGE,{"derivedFrom":subQ5}),-1.0]])]});}
            var Q25;
            {var subQ5=sQuery(id+"F8.wireOp",EDGE,"E136");Q25=makeQuery(id+"F8.imprint","IMPRINT",FACE,{"disambiguationData":[TD([[makeQuery(id+"F8.imprint","IMPRINT",EDGE,{"derivedFrom":subQ5}),1.0]])]});}
            var Q26;
            {var subQ5=sQuery(id+"F8.wireOp",EDGE,"E234");Q26=makeQuery(id+"F8.imprint","IMPRINT",FACE,{"disambiguationData":[TD([[makeQuery(id+"F8.imprint","IMPRINT",EDGE,{"derivedFrom":subQ5}),1.0]])]});}
            var Q27;
            {var subQ5=sQuery(id+"F8.wireOp",EDGE,"E234");Q27=makeQuery(id+"F8.imprint","IMPRINT",FACE,{"disambiguationData":[TD([[makeQuery(id+"F8.imprint","IMPRINT",EDGE,{"derivedFrom":subQ5}),-1.0]])]});}
            var Q28;
            {var subQ3=sQuery(id+"F8.wireOp",EDGE,"E167");Q28=makeQuery(id+"F8.imprint","IMPRINT",FACE,{"disambiguationData":[TD([[makeQuery(id+"F8.imprint","IMPRINT",EDGE,{"derivedFrom":subQ3}),-1.0]])]});}
            var Q29;
            {var subQ5=sQuery(id+"F8.wireOp",EDGE,"E167");Q29=makeQuery(id+"F8.imprint","IMPRINT",FACE,{"disambiguationData":[TD([[makeQuery(id+"F8.imprint","IMPRINT",EDGE,{"derivedFrom":subQ5}),1.0]])]});}
            var Q30;
            {var subQ5=sQuery(id+"F8.wireOp",EDGE,"E164");Q30=makeQuery(id+"F8.imprint","IMPRINT",FACE,{"disambiguationData":[TD([[makeQuery(id+"F8.imprint","IMPRINT",EDGE,{"derivedFrom":subQ5}),1.0]])]});}
            var Q31;
            {var subQ5=sQuery(id+"F8.wireOp",EDGE,"E164");Q31=makeQuery(id+"F8.imprint","IMPRINT",FACE,{"disambiguationData":[TD([[makeQuery(id+"F8.imprint","IMPRINT",EDGE,{"derivedFrom":subQ5}),-1.0]])]});}
            var Q32;
            {var subQ0=sQuery(id+"F8.wireOp",EDGE,"E320");Q32=makeQuery(id+"F8.imprint","IMPRINT",FACE,{"disambiguationData":[TD([[makeQuery(id+"F8.imprint","IMPRINT",EDGE,{"derivedFrom":subQ0}),1.0]])]});}
            var Q33;
            {var subQ0=sQuery(id+"F8.wireOp",EDGE,"E316");Q33=makeQuery(id+"F8.imprint","IMPRINT",FACE,{"disambiguationData":[TD([[makeQuery(id+"F8.imprint","IMPRINT",EDGE,{"derivedFrom":subQ0}),-1.0]])]});}
            extrude(context, id + "F24", {"entities" : qUnion([Q0, Q1, Q2, Q3, Q4, Q5, Q6, Q7, Q8, Q9, Q10, Q11, Q12, Q13, Q14, Q15, Q16, Q17, Q18, Q19, Q20, Q21, Q22, Q23, Q24, Q25, Q26, Q27, Q28, Q29, Q30, Q31, Q32, Q33]), "operationType" : NewBodyOperationType.ADD, "depth" : 2743.2 * mm, "offsetDistance" : 25.4 * mm, "hasSecondDirection" : true, "secondDirectionOppositeDirection" : true, "secondDirectionDepth" : -1981.2 * mm});
        }
        {
            var Q0;
            {var subQ3=sQuery(id+"F8.wireOp",EDGE,"E217");Q0=makeQuery(id+"F8.imprint","IMPRINT",FACE,{"disambiguationData":[TD([[makeQuery(id+"F8.imprint","IMPRINT",EDGE,{"derivedFrom":subQ3}),-1.0]])]});}
            extrude(context, id + "F25", {"entities" : qUnion([Q0]), "operationType" : NewBodyOperationType.ADD, "depth" : 914.4 * mm, "offsetDistance" : 25.4 * mm});
        }
        {
            var Q0;
            {var subQ5=sQuery(id+"F8.wireOp",EDGE,"E318");Q0=makeQuery(id+"F8.imprint","IMPRINT",FACE,{"disambiguationData":[TD([[makeQuery(id+"F8.imprint","IMPRINT",EDGE,{"derivedFrom":subQ5}),-1.0]])]});}
            var Q1;
            {var subQ5=sQuery(id+"F8.wireOp",EDGE,"E319");Q1=makeQuery(id+"F8.imprint","IMPRINT",FACE,{"disambiguationData":[TD([[makeQuery(id+"F8.imprint","IMPRINT",EDGE,{"derivedFrom":subQ5}),1.0]])]});}
            var Q2;
            {var subQ5=sQuery(id+"F8.wireOp",EDGE,"E260");Q2=makeQuery(id+"F8.imprint","IMPRINT",FACE,{"disambiguationData":[TD([[makeQuery(id+"F8.imprint","IMPRINT",EDGE,{"derivedFrom":subQ5}),1.0]])]});}
            var Q3;
            {var subQ5=sQuery(id+"F8.wireOp",EDGE,"E260");Q3=makeQuery(id+"F8.imprint","IMPRINT",FACE,{"disambiguationData":[TD([[makeQuery(id+"F8.imprint","IMPRINT",EDGE,{"derivedFrom":subQ5}),-1.0]])]});}
            extrude(context, id + "F26", {"entities" : qUnion([Q0, Q1, Q2, Q3]), "operationType" : NewBodyOperationType.ADD, "depth" : 2743.2 * mm, "offsetDistance" : 25.4 * mm, "hasSecondDirection" : true, "secondDirectionOppositeDirection" : true, "secondDirectionDepth" : -2133.6 * mm});
        }
        {
            var Q0;
            {var subQ5=sQuery(id+"F8.wireOp",EDGE,"E226");Q0=makeQuery(id+"F8.imprint","IMPRINT",FACE,{"disambiguationData":[TD([[makeQuery(id+"F8.imprint","IMPRINT",EDGE,{"derivedFrom":subQ5}),1.0]])]});}
            var Q1;
            {var subQ5=sQuery(id+"F8.wireOp",EDGE,"E226");Q1=makeQuery(id+"F8.imprint","IMPRINT",FACE,{"disambiguationData":[TD([[makeQuery(id+"F8.imprint","IMPRINT",EDGE,{"derivedFrom":subQ5}),-1.0]])]});}
            extrude(context, id + "F27", {"entities" : qUnion([Q0, Q1]), "operationType" : NewBodyOperationType.ADD, "depth" : 2743.2 * mm, "offsetDistance" : 25.4 * mm, "hasSecondDirection" : true, "secondDirectionOppositeDirection" : true, "secondDirectionDepth" : -2438.4 * mm});
        }
        {
            var Q0;
            {var subQ0=sQuery(id+"F8.wireOp",EDGE,"E70");Q0=makeQuery(id+"F8.imprint","IMPRINT",FACE,{"disambiguationData":[TD([[makeQuery(id+"F8.imprint","IMPRINT",EDGE,{"derivedFrom":subQ0}),-1.0]])]});}
            var sketch = newSketch(context, id + "F28", { "sketchPlane" : qUnion([Q0])});
            skLineSegment(sketch, "E322.0", {"start": v(21018.84, -92202.9) * mm, "end": v(21036.7, -92128.83) * mm});
            skLineSegment(sketch, "E323.0", {"start": v(21519, -90128.76) * mm, "end": v(21741.24, -90182.35) * mm});
            skLineSegment(sketch, "E324.0", {"start": v(20619.6, -88657.73) * mm, "end": v(19476.35, -93398.63) * mm});
            skLineSegment(sketch, "E325.0", {"start": v(24175.27, -89515.16) * mm, "end": v(20619.6, -88657.73) * mm});
            skLineSegment(sketch, "E326.0", {"start": v(23032.02, -94256.07) * mm, "end": v(24175.27, -89515.16) * mm});
            skLineSegment(sketch, "E327", {"start": v(21519, -90128.76) * mm, "end": v(20333.78, -89842.95) * mm});
            skLineSegment(sketch, "E328", {"start": v(21465.42, -90351) * mm, "end": v(20280.2, -90065.18) * mm});
            skLineSegment(sketch, "E329", {"start": v(20226.6, -90287.41) * mm, "end": v(21411.83, -90573.22) * mm});
            skLineSegment(sketch, "E330", {"start": v(20173.01, -90509.64) * mm, "end": v(21358.24, -90795.45) * mm});
            skLineSegment(sketch, "E331", {"start": v(20119.42, -90731.87) * mm, "end": v(21304.65, -91017.68) * mm});
            skLineSegment(sketch, "E332", {"start": v(20065.83, -90954.1) * mm, "end": v(21251.06, -91239.91) * mm});
            skLineSegment(sketch, "E333", {"start": v(20012.24, -91176.33) * mm, "end": v(21197.47, -91462.14) * mm});
            skLineSegment(sketch, "E334", {"start": v(19958.65, -91398.56) * mm, "end": v(21143.88, -91684.37) * mm});
            skLineSegment(sketch, "E335", {"start": v(19905.06, -91620.8) * mm, "end": v(21090.29, -91906.6) * mm});
            skLineSegment(sketch, "E336", {"start": v(21465.42, -90351) * mm, "end": v(21519, -90128.76) * mm});
            skLineSegment(sketch, "E337", {"start": v(21411.83, -90573.22) * mm, "end": v(21465.42, -90351) * mm});
            skLineSegment(sketch, "E338", {"start": v(21358.24, -90795.45) * mm, "end": v(21411.83, -90573.22) * mm});
            skLineSegment(sketch, "E339", {"start": v(21304.65, -91017.68) * mm, "end": v(21358.24, -90795.45) * mm});
            skLineSegment(sketch, "E340", {"start": v(21251.06, -91239.91) * mm, "end": v(21251.06, -91239.91) * mm});
            skLineSegment(sketch, "E341", {"start": v(21143.88, -91684.37) * mm, "end": v(21197.47, -91462.14) * mm});
            skLineSegment(sketch, "E342", {"start": v(21090.29, -91906.6) * mm, "end": v(21143.88, -91684.37) * mm});
            skLineSegment(sketch, "E343", {"start": v(21304.65, -91017.68) * mm, "end": v(21251.06, -91239.91) * mm});
            skLineSegment(sketch, "E344", {"start": v(21197.47, -91462.14) * mm, "end": v(21251.06, -91239.91) * mm});
            skLineSegment(sketch, "E345", {"start": v(21036.7, -92128.83) * mm, "end": v(19851.47, -91843.02) * mm});
            skLineSegment(sketch, "E346", {"start": v(21036.7, -92128.83) * mm, "end": v(21090.29, -91906.6) * mm});
            skLineSegment(sketch, "E347", {"start": v(21519, -90128.76) * mm, "end": v(21804.82, -88943.54) * mm});
            skLineSegment(sketch, "E348", {"start": v(22027.05, -88997.13) * mm, "end": v(21741.24, -90182.35) * mm});
            skLineSegment(sketch, "E349", {"start": v(22249.28, -89050.72) * mm, "end": v(21963.47, -90235.94) * mm});
            skLineSegment(sketch, "E350", {"start": v(21741.24, -90182.35) * mm, "end": v(21963.47, -90235.94) * mm});
            skLineSegment(sketch, "E351", {"start": v(21963.47, -90235.94) * mm, "end": v(22185.7, -90289.53) * mm});
            skLineSegment(sketch, "E352", {"start": v(22185.7, -90289.53) * mm, "end": v(22471.5, -89104.3) * mm});
            skLineSegment(sketch, "E353", {"start": v(22185.7, -90289.53) * mm, "end": v(23889.46, -90700.39) * mm});
            skSolve(sketch);
        }
        {
            var Q0;
            {var subQ0=sQuery(id+"F28.wireOp",EDGE,"E335");Q0=makeQuery(id+"F28.imprint","IMPRINT",FACE,{"disambiguationData":[TD([[makeQuery(id+"F28.imprint","IMPRINT",EDGE,{"derivedFrom":subQ0}),-1.0]])]});}
            extrude(context, id + "F29", {"entities" : qUnion([Q0]), "operationType" : NewBodyOperationType.ADD, "depth" : 203.2 * mm, "offsetDistance" : 25.4 * mm});
        }
        {
            var Q0;
            {var subQ0=sQuery(id+"F28.wireOp",EDGE,"E334");Q0=makeQuery(id+"F28.imprint","IMPRINT",FACE,{"disambiguationData":[TD([[makeQuery(id+"F28.imprint","IMPRINT",EDGE,{"derivedFrom":subQ0}),-1.0]])]});}
            extrude(context, id + "F30", {"entities" : qUnion([Q0]), "operationType" : NewBodyOperationType.ADD, "depth" : 406.4 * mm, "offsetDistance" : 25.4 * mm});
        }
        {
            var Q0;
            {var subQ0=sQuery(id+"F28.wireOp",EDGE,"E333");Q0=makeQuery(id+"F28.imprint","IMPRINT",FACE,{"disambiguationData":[TD([[makeQuery(id+"F28.imprint","IMPRINT",EDGE,{"derivedFrom":subQ0}),-1.0]])]});}
            extrude(context, id + "F31", {"entities" : qUnion([Q0]), "operationType" : NewBodyOperationType.ADD, "depth" : 609.6 * mm, "offsetDistance" : 25.4 * mm});
        }
        {
            var Q0;
            {var subQ0=sQuery(id+"F28.wireOp",EDGE,"E332");Q0=makeQuery(id+"F28.imprint","IMPRINT",FACE,{"disambiguationData":[TD([[makeQuery(id+"F28.imprint","IMPRINT",EDGE,{"derivedFrom":subQ0}),-1.0]])]});}
            extrude(context, id + "F32", {"entities" : qUnion([Q0]), "operationType" : NewBodyOperationType.ADD, "depth" : 812.8 * mm, "offsetDistance" : 25.4 * mm});
        }
        {
            var Q0;
            {var subQ0=sQuery(id+"F28.wireOp",EDGE,"E331");Q0=makeQuery(id+"F28.imprint","IMPRINT",FACE,{"disambiguationData":[TD([[makeQuery(id+"F28.imprint","IMPRINT",EDGE,{"derivedFrom":subQ0}),-1.0]])]});}
            extrude(context, id + "F33", {"entities" : qUnion([Q0]), "operationType" : NewBodyOperationType.ADD, "depth" : 1016 * mm, "offsetDistance" : 25.4 * mm});
        }
        {
            var Q0;
            {var subQ0=sQuery(id+"F28.wireOp",EDGE,"E330");Q0=makeQuery(id+"F28.imprint","IMPRINT",FACE,{"disambiguationData":[TD([[makeQuery(id+"F28.imprint","IMPRINT",EDGE,{"derivedFrom":subQ0}),-1.0]])]});}
            extrude(context, id + "F34", {"entities" : qUnion([Q0]), "operationType" : NewBodyOperationType.ADD, "depth" : 1219.2 * mm, "offsetDistance" : 25.4 * mm});
        }
        {
            var Q0;
            {var subQ0=sQuery(id+"F28.wireOp",EDGE,"E329");Q0=makeQuery(id+"F28.imprint","IMPRINT",FACE,{"disambiguationData":[TD([[makeQuery(id+"F28.imprint","IMPRINT",EDGE,{"derivedFrom":subQ0}),-1.0]])]});}
            extrude(context, id + "F35", {"entities" : qUnion([Q0]), "operationType" : NewBodyOperationType.ADD, "depth" : 1422.4 * mm, "offsetDistance" : 25.4 * mm});
        }
        {
            var Q0;
            {var subQ0=sQuery(id+"F28.wireOp",EDGE,"E328");Q0=makeQuery(id+"F28.imprint","IMPRINT",FACE,{"disambiguationData":[TD([[makeQuery(id+"F28.imprint","IMPRINT",EDGE,{"derivedFrom":subQ0}),1.0]])]});}
            extrude(context, id + "F36", {"entities" : qUnion([Q0]), "operationType" : NewBodyOperationType.ADD, "depth" : 1625.6 * mm, "offsetDistance" : 25.4 * mm});
        }
        {
            var Q0;
            {var subQ0=sQuery(id+"F28.wireOp",EDGE,"E327");Q0=makeQuery(id+"F28.imprint","IMPRINT",FACE,{"disambiguationData":[TD([[makeQuery(id+"F28.imprint","IMPRINT",EDGE,{"derivedFrom":subQ0}),1.0]])]});}
            extrude(context, id + "F37", {"entities" : qUnion([Q0]), "operationType" : NewBodyOperationType.ADD, "depth" : 1828.8 * mm, "offsetDistance" : 25.4 * mm});
        }
        {
            var Q0;
            {var subQ3=sQuery(id+"F28.wireOp",EDGE,"E327");Q0=makeQuery(id+"F28.imprint","IMPRINT",FACE,{"disambiguationData":[TD([[makeQuery(id+"F28.imprint","IMPRINT",EDGE,{"derivedFrom":subQ3}),-1.0]])]});}
            extrude(context, id + "F38", {"entities" : qUnion([Q0]), "operationType" : NewBodyOperationType.ADD, "depth" : 2032 * mm, "offsetDistance" : 25.4 * mm});
        }
        {
            var Q0;
            Q0=makeQuery(id+"F28.imprint","IMPRINT",FACE,{"disambiguationData":[TD([[makeQuery(id+"F28.imprint","IMPRINT",EDGE,{"derivedFrom":sQuery(id+"F28.wireOp",EDGE,"E323.0")}),1.0]])]});
            extrude(context, id + "F39", {"entities" : qUnion([Q0]), "operationType" : NewBodyOperationType.ADD, "depth" : 2235.2 * mm, "offsetDistance" : 25.4 * mm});
        }
        {
            var Q0;
            {var subQ0=sQuery(id+"F28.wireOp",EDGE,"E348");Q0=makeQuery(id+"F28.imprint","IMPRINT",FACE,{"disambiguationData":[TD([[makeQuery(id+"F28.imprint","IMPRINT",EDGE,{"derivedFrom":subQ0}),1.0]])]});}
            extrude(context, id + "F40", {"entities" : qUnion([Q0]), "operationType" : NewBodyOperationType.ADD, "depth" : 2438.4 * mm, "offsetDistance" : 25.4 * mm});
        }
        {
            var Q0;
            {var subQ0=sQuery(id+"F28.wireOp",EDGE,"E349");Q0=makeQuery(id+"F28.imprint","IMPRINT",FACE,{"disambiguationData":[TD([[makeQuery(id+"F28.imprint","IMPRINT",EDGE,{"derivedFrom":subQ0}),1.0]])]});}
            extrude(context, id + "F41", {"entities" : qUnion([Q0]), "operationType" : NewBodyOperationType.ADD, "depth" : 2641.6 * mm, "offsetDistance" : 25.4 * mm});
        }
        {
            var Q0;
            {var subQ2=sQuery(id+"F28.wireOp",EDGE,"E352");Q0=makeQuery(id+"F28.imprint","IMPRINT",FACE,{"disambiguationData":[TD([[makeQuery(id+"F28.imprint","IMPRINT",EDGE,{"derivedFrom":subQ2}),-1.0]])]});}
            extrude(context, id + "F42", {"entities" : qUnion([Q0]), "operationType" : NewBodyOperationType.ADD, "depth" : 2743.2 * mm, "offsetDistance" : 25.4 * mm});
        }
        {
            var Q0;
            {var subQ0=sQuery(id+"F8.wireOp",EDGE,"E67");Q0=makeQuery(id+"F9.opExtrude","SWEPT_FACE",FACE,{"disambiguationData":[OSD([subQ0]),TDD([makeQuery(id+"F8.imprint","IMPRINT",EDGE,{"disambiguationData":[TD([[makeQuery(id+"F8.imprint","INTERSECT",VERTEX,{"derivedFrom":[subQ0,sQuery(id+"F8.wireOp",EDGE,"E80")]}),-1.0]])],"derivedFrom":subQ0})])]});}
            var sketch = newSketch(context, id + "F43", { "sketchPlane" : qUnion([Q0])});
            skLineSegment(sketch, "E354.0.0", {"start": v(-44486.27, 304.8) * mm, "end": v(-43267.07, 304.8) * mm});
            skLineSegment(sketch, "E354.0.1", {"start": v(-43267.07, 304.8) * mm, "end": v(-43267.07, 3048) * mm});
            skLineSegment(sketch, "E354.0.2", {"start": v(-43267.07, 3048) * mm, "end": v(-44486.27, 3048) * mm});
            skLineSegment(sketch, "E354.0.3", {"start": v(-44486.27, 3048) * mm, "end": v(-44486.27, 304.8) * mm});
            skLineSegment(sketch, "E355", {"start": v(-44486.27, 2743.2) * mm, "end": v(-43267.07, 2743.2) * mm});
            skSolve(sketch);
        }
        {
            var Q0;
            {var subQ0=sQuery(id+"F43.wireOp",EDGE,"E354.0.0");Q0=makeQuery(id+"F43.imprint","IMPRINT",FACE,{"disambiguationData":[TD([[makeQuery(id+"F43.imprint","IMPRINT",EDGE,{"derivedFrom":subQ0}),1.0]])]});}
            extrude(context, id + "F44", {"entities" : qUnion([Q0]), "operationType" : NewBodyOperationType.REMOVE, "oppositeDirection" : true, "depth" : 1397 * mm, "offsetDistance" : 25.4 * mm});
        }
        {
            var Q0;
            {var subQ0=sQuery(id+"F8.wireOp",EDGE,"E80");Q0=makeQuery(id+"F44.boolean.opBoolean","MERGE",FACE,{"derivedFrom":[makeQuery(id+"F24.boolean.opBoolean","MERGE",FACE,{"derivedFrom":[makeQuery(id+"F9.opExtrude","SWEPT_FACE",FACE,{"disambiguationData":[OSD([subQ0]),TDD([makeQuery(id+"F8.imprint","IMPRINT",EDGE,{"disambiguationData":[TD([[makeQuery(id+"F8.imprint","INTERSECT",VERTEX,{"derivedFrom":[sQuery(id+"F8.wireOp",EDGE,"E79"),subQ0]}),-1.0]])],"derivedFrom":subQ0})])]}),makeQuery(id+"F9.opExtrude","SWEPT_FACE",FACE,{"disambiguationData":[OSD([subQ0]),TDD([makeQuery(id+"F8.imprint","IMPRINT",EDGE,{"disambiguationData":[TD([[makeQuery(id+"F8.imprint","INTERSECT",VERTEX,{"derivedFrom":[sQuery(id+"F8.wireOp",EDGE,"E67"),subQ0]}),1.0]])],"derivedFrom":subQ0})])]}),makeQuery(id+"F24.opExtrude","SWEPT_FACE",FACE,{"disambiguationData":[OSD([subQ0])]})]}),makeQuery(id+"F9.opExtrude","SWEPT_FACE",FACE,{"disambiguationData":[OSD([sQuery(id+"F8.wireOp",EDGE,"E68")])]})],"fromTools":[makeQuery(id+"F44.opExtrude","SWEPT_FACE",FACE,{"disambiguationData":[OSD([sQuery(id+"F43.wireOp",EDGE,"E354.0.3")])]})]});}
            var sketch = newSketch(context, id + "F45", { "sketchPlane" : qUnion([Q0])});
            skLineSegment(sketch, "E356.0", {"start": v(86230.23, 304.8) * mm, "end": v(81353.43, 304.8) * mm});
            skLineSegment(sketch, "E357.0", {"start": v(86230.23, 3048) * mm, "end": v(86230.23, 304.8) * mm});
            skLineSegment(sketch, "E358.0", {"start": v(86230.23, 3048) * mm, "end": v(82572.63, 3048) * mm});
            skLineSegment(sketch, "E359", {"start": v(84604.63, 304.8) * mm, "end": v(84604.63, 2743.2) * mm});
            skLineSegment(sketch, "E360", {"start": v(84604.63, 2743.2) * mm, "end": v(86027.03, 2743.2) * mm});
            skLineSegment(sketch, "E361", {"start": v(86027.03, 2743.2) * mm, "end": v(86027.03, 304.8) * mm});
            skArc(sketch, "E362", {"start": v(86027.03, 2540) * mm, "mid": v(85315.83, 2743.2) * mm, "end": v(84604.63, 2540) * mm});
            skLineSegment(sketch, "E363", {"start": v(84604.63, 2540) * mm, "end": v(86027.03, 2540) * mm, "construction": true});
            skSolve(sketch);
        }
        {
            var Q0;
            {var subQ1=sQuery(id+"F45.wireOp",EDGE,"E356.0");var subQ5=sQuery(id+"F45.wireOp",EDGE,"E359");var subQ6=makeQuery(id+"F45.imprint","INTERSECT",VERTEX,{"derivedFrom":[subQ1,subQ5]});Q0=makeQuery(id+"F45.imprint","IMPRINT",FACE,{"disambiguationData":[TD([[makeQuery(id+"F45.imprint","IMPRINT",EDGE,{"disambiguationData":[TD([[subQ6,-1.0]])],"derivedFrom":subQ1}),1.0]])]});}
            extrude(context, id + "F46", {"entities" : qUnion([Q0]), "operationType" : NewBodyOperationType.REMOVE, "oppositeDirection" : true, "depth" : 304.8 * mm, "offsetDistance" : 25.4 * mm});
        }
        {
            var Q0;
            {var subQ5=sQuery(id+"F8.wireOp",EDGE,"E158.trimOffspring");Q0=makeQuery(id+"F8.imprint","IMPRINT",FACE,{"disambiguationData":[TD([[makeQuery(id+"F8.imprint","IMPRINT",EDGE,{"derivedFrom":subQ5}),-1.0]])]});}
            var Q1;
            {var subQ5=sQuery(id+"F8.wireOp",EDGE,"E148");Q1=makeQuery(id+"F8.imprint","IMPRINT",FACE,{"disambiguationData":[TD([[makeQuery(id+"F8.imprint","IMPRINT",EDGE,{"derivedFrom":subQ5}),-1.0]])]});}
            extrude(context, id + "F47", {"entities" : qUnion([Q0, Q1]), "operationType" : NewBodyOperationType.ADD, "depth" : 2438.4 * mm, "offsetDistance" : 25.4 * mm});
        }
        {
            var Q0;
            {var subQ2=sQuery(id+"F8.wireOp",EDGE,"E158.trimOffspring");Q0=makeQuery(id+"F8.imprint","IMPRINT",FACE,{"disambiguationData":[TD([[makeQuery(id+"F8.imprint","IMPRINT",EDGE,{"derivedFrom":subQ2}),1.0]])]});}
            var Q1;
            {var subQ0=sQuery(id+"F8.wireOp",EDGE,"E147");Q1=makeQuery(id+"F8.imprint","IMPRINT",FACE,{"disambiguationData":[TD([[makeQuery(id+"F8.imprint","IMPRINT",EDGE,{"derivedFrom":subQ0}),-1.0]])]});}
            extrude(context, id + "F48", {"entities" : qUnion([Q0, Q1]), "operationType" : NewBodyOperationType.ADD, "depth" : 406.4 * mm, "offsetDistance" : 25.4 * mm});
        }
        {
            var Q0;
            {var subQ3=sQuery(id+"F8.wireOp",EDGE,"E161");Q0=makeQuery(id+"F8.imprint","IMPRINT",FACE,{"disambiguationData":[TD([[makeQuery(id+"F8.imprint","IMPRINT",EDGE,{"derivedFrom":subQ3}),1.0]])]});}
            var Q1;
            {var subQ0=sQuery(id+"F8.wireOp",EDGE,"E115");Q1=makeQuery(id+"F8.imprint","IMPRINT",FACE,{"disambiguationData":[TD([[makeQuery(id+"F8.imprint","IMPRINT",EDGE,{"derivedFrom":subQ0}),1.0]])]});}
            extrude(context, id + "F49", {"entities" : qUnion([Q0, Q1]), "operationType" : NewBodyOperationType.ADD, "depth" : 914.4 * mm, "offsetDistance" : 25.4 * mm});
        }
        {
            var Q0;
            Q0=makeQuery(id+"F49.opExtrude","CAP_FACE",FACE,{"disambiguationData":[OSD([sQuery(id+"F8.wireOp",EDGE,"E59"),sQuery(id+"F8.wireOp",EDGE,"E61"),sQuery(id+"F8.wireOp",EDGE,"E114"),sQuery(id+"F8.wireOp",EDGE,"E161")])],"isStart":false});
            var sketch = newSketch(context, id + "F50", { "sketchPlane" : qUnion([Q0])});
            skLineSegment(sketch, "E364.0.0", {"start": v(15884.8, -80500.56) * mm, "end": v(15741.9, -81093.17) * mm});
            skLineSegment(sketch, "E364.0.1", {"start": v(15741.9, -81093.17) * mm, "end": v(18112.35, -81664.8) * mm});
            skLineSegment(sketch, "E364.0.2", {"start": v(18112.35, -81664.8) * mm, "end": v(18255.26, -81072.19) * mm});
            skLineSegment(sketch, "E364.0.3", {"start": v(18255.26, -81072.19) * mm, "end": v(15884.8, -80500.56) * mm});
            skLineSegment(sketch, "E365.0.0", {"start": v(17853.33, -82738.9) * mm, "end": v(15482.88, -82167.29) * mm});
            skLineSegment(sketch, "E365.0.1", {"start": v(15482.88, -82167.29) * mm, "end": v(15339.97, -82759.9) * mm});
            skLineSegment(sketch, "E365.0.2", {"start": v(15339.97, -82759.9) * mm, "end": v(17710.43, -83331.52) * mm});
            skLineSegment(sketch, "E365.0.3", {"start": v(17710.43, -83331.52) * mm, "end": v(17853.33, -82738.9) * mm});
            skLineSegment(sketch, "E366", {"start": v(15813.35, -80796.87) * mm, "end": v(18183.8, -81368.5) * mm});
            skLineSegment(sketch, "E367", {"start": v(17781.88, -83035.22) * mm, "end": v(15411.43, -82463.6) * mm});
            skSolve(sketch);
        }
        {
            var Q0;
            {var subQ0=sQuery(id+"F50.wireOp",EDGE,"E364.0.3");Q0=makeQuery(id+"F50.imprint","IMPRINT",FACE,{"disambiguationData":[TD([[makeQuery(id+"F50.imprint","IMPRINT",EDGE,{"derivedFrom":subQ0}),-1.0]])]});}
            var Q1;
            {var subQ0=sQuery(id+"F50.wireOp",EDGE,"E365.0.2");Q1=makeQuery(id+"F50.imprint","IMPRINT",FACE,{"disambiguationData":[TD([[makeQuery(id+"F50.imprint","IMPRINT",EDGE,{"derivedFrom":subQ0}),1.0]])]});}
            var Q2;
            {var subQ0=sQuery(id+"F8.wireOp",EDGE,"E225");var subQ1=sQuery(id+"F8.wireOp",EDGE,"E224");var subQ2=sQuery(id+"F8.wireOp",EDGE,"E117");var subQ3=sQuery(id+"F8.wireOp",EDGE,"E55.9");var subQ4=sQuery(id+"F8.wireOp",EDGE,"E319");var subQ5=sQuery(id+"F8.wireOp",EDGE,"E318");var subQ6=sQuery(id+"F8.wireOp",EDGE,"E55.0");var subQ7=sQuery(id+"F8.wireOp",EDGE,"E52");var subQ8=sQuery(id+"F8.wireOp",EDGE,"E259");var subQ9=sQuery(id+"F8.wireOp",EDGE,"E258");var subQ10=sQuery(id+"F8.wireOp",EDGE,"E55.10");var subQ11=sQuery(id+"F8.wireOp",EDGE,"E50");var subQ12=sQuery(id+"F8.wireOp",EDGE,"E233");var subQ13=sQuery(id+"F8.wireOp",EDGE,"E232");var subQ14=sQuery(id+"F8.wireOp",EDGE,"E221");var subQ15=sQuery(id+"F8.wireOp",EDGE,"E216");var subQ16=sQuery(id+"F8.wireOp",EDGE,"E205");var subQ17=sQuery(id+"F8.wireOp",EDGE,"E204");var subQ18=sQuery(id+"F8.wireOp",EDGE,"E202");var subQ19=sQuery(id+"F8.wireOp",EDGE,"E200");var subQ20=sQuery(id+"F8.wireOp",EDGE,"E195");var subQ21=sQuery(id+"F8.wireOp",EDGE,"E194");var subQ22=sQuery(id+"F8.wireOp",EDGE,"E173");var subQ23=sQuery(id+"F8.wireOp",EDGE,"E172");var subQ24=sQuery(id+"F8.wireOp",EDGE,"E186");var subQ25=sQuery(id+"F8.wireOp",EDGE,"E185");var subQ26=sQuery(id+"F8.wireOp",EDGE,"E135");var subQ27=sQuery(id+"F8.wireOp",EDGE,"E134");var subQ28=sQuery(id+"F8.wireOp",EDGE,"E123");var subQ29=sQuery(id+"F8.wireOp",EDGE,"E122");var subQ30=sQuery(id+"F8.wireOp",EDGE,"E144");var subQ31=sQuery(id+"F8.wireOp",EDGE,"E143");var subQ32=sQuery(id+"F8.wireOp",EDGE,"E121");var subQ33=sQuery(id+"F8.wireOp",EDGE,"E120");var subQ34=sQuery(id+"F8.wireOp",EDGE,"E220.trimOffspring");var subQ35=sQuery(id+"F8.wireOp",EDGE,"E153");var subQ36=sQuery(id+"F8.wireOp",EDGE,"E152");var subQ37=sQuery(id+"F8.wireOp",EDGE,"E118");var subQ38=sQuery(id+"F8.wireOp",EDGE,"E317");var subQ39=sQuery(id+"F8.wireOp",EDGE,"E316");var subQ40=sQuery(id+"F8.wireOp",EDGE,"E215");var subQ41=sQuery(id+"F8.wireOp",EDGE,"E114");var subQ42=sQuery(id+"F8.wireOp",EDGE,"E166");var subQ43=sQuery(id+"F8.wireOp",EDGE,"E165");var subQ44=sQuery(id+"F8.wireOp",EDGE,"E272");var subQ45=sQuery(id+"F8.wireOp",EDGE,"E270");var subQ46=sQuery(id+"F8.wireOp",EDGE,"E84");var subQ47=sQuery(id+"F8.wireOp",EDGE,"E82");var subQ48=sQuery(id+"F8.wireOp",EDGE,"E267");var subQ49=sQuery(id+"F8.wireOp",EDGE,"E266");var subQ50=sQuery(id+"F8.wireOp",EDGE,"E109");var subQ51=sQuery(id+"F8.wireOp",EDGE,"E108");var subQ52=sQuery(id+"F8.wireOp",EDGE,"E80");var subQ53=sQuery(id+"F8.wireOp",EDGE,"E77");var subQ54=sQuery(id+"F8.wireOp",EDGE,"E105");var subQ55=sQuery(id+"F8.wireOp",EDGE,"E104");var subQ56=sQuery(id+"F8.wireOp",EDGE,"E74");var subQ57=sQuery(id+"F8.wireOp",EDGE,"E73");var subQ58=sQuery(id+"F8.wireOp",EDGE,"E163");var subQ59=sQuery(id+"F8.wireOp",EDGE,"E162");var subQ60=sQuery(id+"F8.wireOp",EDGE,"E60");var subQ61=sQuery(id+"F8.wireOp",EDGE,"E59");var subQ62=sQuery(id+"F8.wireOp",EDGE,"E321");var subQ63=sQuery(id+"F8.wireOp",EDGE,"E320");var subQ64=sQuery(id+"F8.wireOp",EDGE,"E58.0");var subQ65=sQuery(id+"F8.wireOp",EDGE,"E57");var subQ66=sQuery(id+"F8.wireOp",EDGE,"E92");var subQ67=sQuery(id+"F8.wireOp",EDGE,"E90");var subQ68=sQuery(id+"F8.wireOp",EDGE,"E103.trimOffspring");var subQ69=sQuery(id+"F8.wireOp",EDGE,"E53");Q2=makeQuery(id+"F42.boolean.opBoolean","MERGE",FACE,{"derivedFrom":[makeQuery(id+"F27.boolean.opBoolean","MERGE",FACE,{"derivedFrom":[makeQuery(id+"F26.boolean.opBoolean","MERGE",FACE,{"derivedFrom":[makeQuery(id+"F24.boolean.opBoolean","MERGE",FACE,{"derivedFrom":[makeQuery(id+"F9.opExtrude","CAP_FACE",FACE,{"disambiguationData":[OSD([sQuery(id+"F8.wireOp",EDGE,"E27"),sQuery(id+"F8.wireOp",EDGE,"E45"),sQuery(id+"F8.wireOp",EDGE,"E46"),sQuery(id+"F8.wireOp",EDGE,"E47"),sQuery(id+"F8.wireOp",EDGE,"E48"),sQuery(id+"F8.wireOp",EDGE,"E49"),subQ11,sQuery(id+"F8.wireOp",EDGE,"E51"),subQ7,subQ69,sQuery(id+"F8.wireOp",EDGE,"E54.trimOffspring"),subQ6,sQuery(id+"F8.wireOp",EDGE,"E55.1"),sQuery(id+"F8.wireOp",EDGE,"E55.2"),sQuery(id+"F8.wireOp",EDGE,"E55.3"),sQuery(id+"F8.wireOp",EDGE,"E55.4"),sQuery(id+"F8.wireOp",EDGE,"E55.5"),sQuery(id+"F8.wireOp",EDGE,"E55.7"),sQuery(id+"F8.wireOp",EDGE,"E55.8"),subQ3,subQ10,sQuery(id+"F8.wireOp",EDGE,"E55.11"),sQuery(id+"F8.wireOp",EDGE,"E56"),subQ65,subQ64,sQuery(id+"F8.wireOp",EDGE,"E58.1"),sQuery(id+"F8.wireOp",EDGE,"E66"),sQuery(id+"F8.wireOp",EDGE,"E67"),sQuery(id+"F8.wireOp",EDGE,"E68"),sQuery(id+"F8.wireOp",EDGE,"E69"),subQ57,subQ56,sQuery(id+"F8.wireOp",EDGE,"E75"),sQuery(id+"F8.wireOp",EDGE,"E76"),subQ53,sQuery(id+"F8.wireOp",EDGE,"E78.trimOffspring"),sQuery(id+"F8.wireOp",EDGE,"E79"),subQ52,subQ47,subQ46,sQuery(id+"F8.wireOp",EDGE,"E91"),subQ68,subQ55,subQ54,subQ51,subQ50,sQuery(id+"F8.wireOp",EDGE,"E112"),sQuery(id+"F8.wireOp",EDGE,"E113"),subQ41,subQ2,subQ37,sQuery(id+"F8.wireOp",EDGE,"E119"),subQ33,subQ32,subQ29,subQ28,subQ27,subQ26,subQ31,subQ30,subQ36,subQ35,sQuery(id+"F8.wireOp",EDGE,"E171"),subQ23,subQ22,sQuery(id+"F8.wireOp",EDGE,"E174"),sQuery(id+"F8.wireOp",EDGE,"E175"),subQ25,subQ24,sQuery(id+"F8.wireOp",EDGE,"E189"),sQuery(id+"F8.wireOp",EDGE,"E190"),subQ21,subQ20,subQ19,sQuery(id+"F8.wireOp",EDGE,"E201"),subQ18,sQuery(id+"F8.wireOp",EDGE,"E203"),subQ17,subQ16,sQuery(id+"F8.wireOp",EDGE,"E208"),sQuery(id+"F8.wireOp",EDGE,"E209"),sQuery(id+"F8.wireOp",EDGE,"E210.trimOffspring"),sQuery(id+"F8.wireOp",EDGE,"E211.trimOffspring"),subQ40,subQ15,sQuery(id+"F8.wireOp",EDGE,"E217"),sQuery(id+"F8.wireOp",EDGE,"E218"),sQuery(id+"F8.wireOp",EDGE,"E219.trimOffspring"),subQ34,subQ14,sQuery(id+"F8.wireOp",EDGE,"E222"),subQ0,subQ13,subQ12,sQuery(id+"F8.wireOp",EDGE,"E239"),sQuery(id+"F8.wireOp",EDGE,"E240"),sQuery(id+"F8.wireOp",EDGE,"E241"),sQuery(id+"F8.wireOp",EDGE,"E242"),sQuery(id+"F8.wireOp",EDGE,"E256"),sQuery(id+"F8.wireOp",EDGE,"E257"),subQ8,sQuery(id+"F8.wireOp",EDGE,"E261"),subQ48,subQ45,subQ44,sQuery(id+"F8.wireOp",EDGE,"E280"),subQ38,subQ4,subQ62])],"isStart":false}),makeQuery(id+"F9.opExtrude","CAP_FACE",FACE,{"disambiguationData":[OSD([subQ11,subQ3,subQ10,subQ65,subQ64,subQ2,subQ1,subQ9,subQ63])],"isStart":false}),makeQuery(id+"F9.opExtrude","CAP_FACE",FACE,{"disambiguationData":[OSD([subQ7,subQ69,subQ6,sQuery(id+"F8.wireOp",EDGE,"E55.6"),subQ61,subQ60,sQuery(id+"F8.wireOp",EDGE,"E61"),sQuery(id+"F8.wireOp",EDGE,"E62"),sQuery(id+"F8.wireOp",EDGE,"E63"),sQuery(id+"F8.wireOp",EDGE,"E64"),sQuery(id+"F8.wireOp",EDGE,"E65"),sQuery(id+"F8.wireOp",EDGE,"E102"),subQ68,subQ41,subQ58,subQ42,subQ40,sQuery(id+"F8.wireOp",EDGE,"E275"),sQuery(id+"F8.wireOp",EDGE,"E309"),sQuery(id+"F8.wireOp",EDGE,"E313"),sQuery(id+"F8.wireOp",EDGE,"E314"),sQuery(id+"F8.wireOp",EDGE,"E315"),subQ5])],"isStart":false}),makeQuery(id+"F9.opExtrude","CAP_FACE",FACE,{"disambiguationData":[OSD([subQ61,subQ60,subQ67,subQ66,subQ41,sQuery(id+"F8.wireOp",EDGE,"E115"),subQ59,subQ43,sQuery(id+"F8.wireOp",EDGE,"E169"),subQ40,subQ39])],"isStart":false}),makeQuery(id+"F9.opExtrude","CAP_FACE",FACE,{"disambiguationData":[OSD([sQuery(id+"F8.wireOp",EDGE,"E81"),subQ47,sQuery(id+"F8.wireOp",EDGE,"E83"),subQ46,subQ67,subQ66,sQuery(id+"F8.wireOp",EDGE,"E93"),sQuery(id+"F8.wireOp",EDGE,"E170"),sQuery(id+"F8.wireOp",EDGE,"E265"),subQ49])],"isStart":false}),makeQuery(id+"F24.opExtrude","CAP_FACE",FACE,{"disambiguationData":[OSD([subQ65,subQ64,subQ63,subQ62])],"isStart":false}),makeQuery(id+"F24.opExtrude","CAP_FACE",FACE,{"disambiguationData":[OSD([subQ61,subQ60,subQ59,subQ58])],"isStart":false}),makeQuery(id+"F24.opExtrude","CAP_FACE",FACE,{"disambiguationData":[OSD([subQ57,subQ56,subQ55,subQ54])],"isStart":false}),makeQuery(id+"F24.opExtrude","CAP_FACE",FACE,{"disambiguationData":[OSD([subQ53,subQ52,subQ51,subQ50])],"isStart":false}),makeQuery(id+"F24.opExtrude","CAP_FACE",FACE,{"disambiguationData":[OSD([subQ47,subQ46,subQ49,subQ48])],"isStart":false}),makeQuery(id+"F24.opExtrude","CAP_FACE",FACE,{"disambiguationData":[OSD([subQ47,subQ46,subQ45,subQ44])],"isStart":false}),makeQuery(id+"F24.opExtrude","CAP_FACE",FACE,{"disambiguationData":[OSD([subQ41,subQ43,subQ42,subQ40])],"isStart":false}),makeQuery(id+"F24.opExtrude","CAP_FACE",FACE,{"disambiguationData":[OSD([subQ41,subQ40,subQ39,subQ38])],"isStart":false}),makeQuery(id+"F24.opExtrude","CAP_FACE",FACE,{"disambiguationData":[OSD([subQ37,subQ36,subQ35,subQ34])],"isStart":false}),makeQuery(id+"F24.opExtrude","CAP_FACE",FACE,{"disambiguationData":[OSD([subQ33,subQ32,subQ31,subQ30])],"isStart":false}),makeQuery(id+"F24.opExtrude","CAP_FACE",FACE,{"disambiguationData":[OSD([subQ29,subQ28,subQ27,subQ26])],"isStart":false}),makeQuery(id+"F24.opExtrude","CAP_FACE",FACE,{"disambiguationData":[OSD([subQ23,subQ22,subQ25,subQ24])],"isStart":false}),makeQuery(id+"F24.opExtrude","CAP_FACE",FACE,{"disambiguationData":[OSD([subQ23,subQ22,subQ21,subQ20])],"isStart":false}),makeQuery(id+"F24.opExtrude","CAP_FACE",FACE,{"disambiguationData":[OSD([subQ19,subQ18,subQ17,subQ16])],"isStart":false}),makeQuery(id+"F24.opExtrude","CAP_FACE",FACE,{"disambiguationData":[OSD([subQ15,subQ14,subQ13,subQ12])],"isStart":false})]}),makeQuery(id+"F26.opExtrude","CAP_FACE",FACE,{"disambiguationData":[OSD([subQ11,subQ10,subQ9,subQ8])],"isStart":false}),makeQuery(id+"F26.opExtrude","CAP_FACE",FACE,{"disambiguationData":[OSD([subQ7,subQ6,subQ5,subQ4])],"isStart":false})]}),makeQuery(id+"F27.opExtrude","CAP_FACE",FACE,{"disambiguationData":[OSD([subQ3,subQ2,subQ1,subQ0])],"isStart":false})]}),makeQuery(id+"F42.opExtrude","CAP_FACE",FACE,{"disambiguationData":[OSD([sQuery(id+"F28.wireOp",EDGE,"E325.0"),sQuery(id+"F28.wireOp",EDGE,"E326.0"),sQuery(id+"F28.wireOp",EDGE,"E352"),sQuery(id+"F28.wireOp",EDGE,"E353")])],"isStart":false})]});}
            extrude(context, id + "F51", {"entities" : qUnion([Q0, Q1]), "operationType" : NewBodyOperationType.ADD, "depth" : 1524 * mm, "endBoundEntityFace" : qUnion([Q2]), "offsetDistance" : 25.4 * mm});
        }
        {
            var Q0;
            {var subQ0=sQuery(id+"F8.wireOp",EDGE,"E103.trimOffspring");var subQ1=makeQuery(id+"F8.imprint","INTERSECT",VERTEX,{"derivedFrom":[subQ0,sQuery(id+"F8.wireOp",EDGE,"E279")]});var subQ3=makeQuery(id+"F8.imprint","INTERSECT",VERTEX,{"derivedFrom":[subQ0,sQuery(id+"F8.wireOp",EDGE,"E277")]});var subQ4=makeQuery(id+"F8.imprint","INTERSECT",VERTEX,{"derivedFrom":[subQ0,sQuery(id+"F8.wireOp",EDGE,"E278")]});var subQ5=makeQuery(id+"F8.imprint","INTERSECT",VERTEX,{"derivedFrom":[subQ0,sQuery(id+"F8.wireOp",EDGE,"E276")]});Q0=makeQuery(id+"F17.boolean.opBoolean","MERGE",FACE,{"derivedFrom":[makeQuery(id+"F9.opExtrude","SWEPT_FACE",FACE,{"disambiguationData":[OSD([subQ0]),TDD([makeQuery(id+"F8.imprint","IMPRINT",EDGE,{"disambiguationData":[TD([[subQ5,-1.0]])],"derivedFrom":subQ0})])]}),makeQuery(id+"F9.opExtrude","SWEPT_FACE",FACE,{"disambiguationData":[OSD([subQ0]),TDD([makeQuery(id+"F8.imprint","IMPRINT",EDGE,{"disambiguationData":[TD([[subQ4,-1.0]])],"derivedFrom":subQ0})])]}),makeQuery(id+"F9.opExtrude","SWEPT_FACE",FACE,{"disambiguationData":[OSD([subQ0]),TDD([makeQuery(id+"F8.imprint","IMPRINT",EDGE,{"disambiguationData":[TD([[makeQuery(id+"F8.imprint","INTERSECT",VERTEX,{"derivedFrom":[subQ0,sQuery(id+"F8.wireOp",EDGE,"E261")]}),1.0]])],"derivedFrom":subQ0})])]}),makeQuery(id+"F9.opExtrude","SWEPT_FACE",FACE,{"disambiguationData":[OSD([sQuery(id+"F8.wireOp",EDGE,"E55.6"),sQuery(id+"F8.wireOp",EDGE,"E102"),subQ0,sQuery(id+"F8.wireOp",EDGE,"E315")])]}),makeQuery(id+"F17.opExtrude","SWEPT_FACE",FACE,{"disambiguationData":[OSD([subQ0]),TDD([makeQuery(id+"F8.imprint","IMPRINT",EDGE,{"disambiguationData":[TD([[makeQuery(id+"F8.imprint","INTERSECT",VERTEX,{"derivedFrom":[subQ0,sQuery(id+"F8.wireOp",EDGE,"E275")]}),-1.0]])],"derivedFrom":subQ0})])]}),makeQuery(id+"F17.opExtrude","SWEPT_FACE",FACE,{"disambiguationData":[OSD([subQ0]),TDD([makeQuery(id+"F8.imprint","IMPRINT",EDGE,{"disambiguationData":[TD([[subQ3,-1.0]])],"derivedFrom":subQ0})])]}),makeQuery(id+"F17.opExtrude","SWEPT_FACE",FACE,{"disambiguationData":[OSD([subQ0]),TDD([makeQuery(id+"F8.imprint","IMPRINT",EDGE,{"disambiguationData":[TD([[subQ1,-1.0]])],"derivedFrom":subQ0})])]})]});}
            var sketch = newSketch(context, id + "F52", { "sketchPlane" : qUnion([Q0])});
            skLineSegment(sketch, "E368.0.0", {"start": v(37513.97, 304.8) * mm, "end": v(47953.37, 304.8) * mm});
            skLineSegment(sketch, "E368.0.1", {"start": v(47953.37, 304.8) * mm, "end": v(47953.37, 3048) * mm});
            skLineSegment(sketch, "E368.0.2", {"start": v(47953.37, 3048) * mm, "end": v(47267.57, 3048) * mm});
            skLineSegment(sketch, "E368.0.3", {"start": v(47267.57, 3048) * mm, "end": v(47267.57, 914.4) * mm});
            skLineSegment(sketch, "E368.0.4", {"start": v(47267.57, 914.4) * mm, "end": v(46505.57, 914.4) * mm});
            skLineSegment(sketch, "E368.0.5", {"start": v(46505.57, 914.4) * mm, "end": v(46505.57, 3048) * mm});
            skLineSegment(sketch, "E368.0.6", {"start": v(46505.57, 3048) * mm, "end": v(46200.77, 3048) * mm});
            skLineSegment(sketch, "E368.0.7", {"start": v(46200.77, 3048) * mm, "end": v(46200.77, 914.4) * mm});
            skLineSegment(sketch, "E368.0.8", {"start": v(46200.77, 914.4) * mm, "end": v(45438.77, 914.4) * mm});
            skLineSegment(sketch, "E368.0.9", {"start": v(45438.77, 914.4) * mm, "end": v(45438.77, 3048) * mm});
            skLineSegment(sketch, "E368.0.10", {"start": v(45438.77, 3048) * mm, "end": v(45133.97, 3048) * mm});
            skLineSegment(sketch, "E368.0.11", {"start": v(45133.97, 3048) * mm, "end": v(45133.97, 914.4) * mm});
            skLineSegment(sketch, "E368.0.12", {"start": v(45133.97, 914.4) * mm, "end": v(44371.97, 914.4) * mm});
            skLineSegment(sketch, "E368.0.13", {"start": v(44371.97, 914.4) * mm, "end": v(44371.97, 3048) * mm});
            skLineSegment(sketch, "E368.0.14", {"start": v(44371.97, 3048) * mm, "end": v(31570.37, 3048) * mm});
            skLineSegment(sketch, "E368.0.15", {"start": v(31570.37, 3048) * mm, "end": v(31570.37, 304.8) * mm});
            skLineSegment(sketch, "E368.0.16", {"start": v(31570.37, 304.8) * mm, "end": v(36294.77, 304.8) * mm});
            skLineSegment(sketch, "E368.0.17", {"start": v(36294.77, 304.8) * mm, "end": v(36294.77, 2438.4) * mm});
            skLineSegment(sketch, "E368.0.18", {"start": v(36294.77, 2438.4) * mm, "end": v(37513.97, 2438.4) * mm});
            skLineSegment(sketch, "E368.0.19", {"start": v(37513.97, 2438.4) * mm, "end": v(37513.97, 304.8) * mm});
            skLineSegment(sketch, "E369.0", {"start": v(32332.37, 1066.8) * mm, "end": v(35989.97, 1066.8) * mm});
            skLineSegment(sketch, "E370.bottom", {"start": v(32560.97, 2743.2) * mm, "end": v(33322.97, 2743.2) * mm});
            skLineSegment(sketch, "E370.top", {"start": v(32560.97, 914.4) * mm, "end": v(33322.97, 914.4) * mm});
            skLineSegment(sketch, "E370.left", {"start": v(32560.97, 2743.2) * mm, "end": v(32560.97, 914.4) * mm});
            skLineSegment(sketch, "E370.right", {"start": v(33322.97, 2743.2) * mm, "end": v(33322.97, 914.4) * mm});
            skLineSegment(sketch, "E371.bottom", {"start": v(33780.17, 2743.2) * mm, "end": v(34542.17, 2743.2) * mm});
            skLineSegment(sketch, "E371.top", {"start": v(33780.17, 914.4) * mm, "end": v(34542.17, 914.4) * mm});
            skLineSegment(sketch, "E371.left", {"start": v(33780.17, 2743.2) * mm, "end": v(33780.17, 914.4) * mm});
            skLineSegment(sketch, "E371.right", {"start": v(34542.17, 2743.2) * mm, "end": v(34542.17, 914.4) * mm});
            skLineSegment(sketch, "E372.bottom", {"start": v(34999.37, 2743.2) * mm, "end": v(35761.37, 2743.2) * mm});
            skLineSegment(sketch, "E372.top", {"start": v(34999.37, 914.4) * mm, "end": v(35761.37, 914.4) * mm});
            skLineSegment(sketch, "E372.left", {"start": v(34999.37, 2743.2) * mm, "end": v(34999.37, 914.4) * mm});
            skLineSegment(sketch, "E372.right", {"start": v(35761.37, 2743.2) * mm, "end": v(35761.37, 914.4) * mm});
            skSolve(sketch);
        }
        {
            var Q0;
            {var subQ5=sQuery(id+"F52.wireOp",EDGE,"E370.bottom");Q0=makeQuery(id+"F52.imprint","IMPRINT",FACE,{"disambiguationData":[TD([[makeQuery(id+"F52.imprint","IMPRINT",EDGE,{"derivedFrom":subQ5}),-1.0]])]});}
            var Q1;
            {var subQ0=sQuery(id+"F52.wireOp",EDGE,"E370.top");Q1=makeQuery(id+"F52.imprint","IMPRINT",FACE,{"disambiguationData":[TD([[makeQuery(id+"F52.imprint","IMPRINT",EDGE,{"derivedFrom":subQ0}),1.0]])]});}
            var Q2;
            {var subQ0=sQuery(id+"F52.wireOp",EDGE,"E370.left");var subQ1=sQuery(id+"F52.wireOp",EDGE,"E369.0");var subQ2=makeQuery(id+"F52.imprint","INTERSECT",VERTEX,{"derivedFrom":[subQ1,subQ0]});Q2=makeQuery(id+"F52.imprint","IMPRINT",FACE,{"disambiguationData":[TD([[makeQuery(id+"F52.imprint","IMPRINT",EDGE,{"disambiguationData":[TD([[subQ2,-1.0]])],"derivedFrom":subQ1}),-1.0]])]});}
            var Q3;
            {var subQ5=sQuery(id+"F52.wireOp",EDGE,"E371.bottom");Q3=makeQuery(id+"F52.imprint","IMPRINT",FACE,{"disambiguationData":[TD([[makeQuery(id+"F52.imprint","IMPRINT",EDGE,{"derivedFrom":subQ5}),-1.0]])]});}
            var Q4;
            {var subQ5=sQuery(id+"F52.wireOp",EDGE,"E372.bottom");Q4=makeQuery(id+"F52.imprint","IMPRINT",FACE,{"disambiguationData":[TD([[makeQuery(id+"F52.imprint","IMPRINT",EDGE,{"derivedFrom":subQ5}),-1.0]])]});}
            var Q5;
            {var subQ0=sQuery(id+"F52.wireOp",EDGE,"E371.left");var subQ1=sQuery(id+"F52.wireOp",EDGE,"E369.0");var subQ2=makeQuery(id+"F52.imprint","INTERSECT",VERTEX,{"derivedFrom":[subQ1,subQ0]});Q5=makeQuery(id+"F52.imprint","IMPRINT",FACE,{"disambiguationData":[TD([[makeQuery(id+"F52.imprint","IMPRINT",EDGE,{"disambiguationData":[TD([[subQ2,-1.0]])],"derivedFrom":subQ1}),-1.0]])]});}
            var Q6;
            {var subQ0=sQuery(id+"F52.wireOp",EDGE,"E371.top");Q6=makeQuery(id+"F52.imprint","IMPRINT",FACE,{"disambiguationData":[TD([[makeQuery(id+"F52.imprint","IMPRINT",EDGE,{"derivedFrom":subQ0}),1.0]])]});}
            var Q7;
            {var subQ0=sQuery(id+"F52.wireOp",EDGE,"E372.top");Q7=makeQuery(id+"F52.imprint","IMPRINT",FACE,{"disambiguationData":[TD([[makeQuery(id+"F52.imprint","IMPRINT",EDGE,{"derivedFrom":subQ0}),1.0]])]});}
            var Q8;
            {var subQ0=sQuery(id+"F52.wireOp",EDGE,"E372.left");var subQ1=sQuery(id+"F52.wireOp",EDGE,"E369.0");var subQ2=makeQuery(id+"F52.imprint","INTERSECT",VERTEX,{"derivedFrom":[subQ1,subQ0]});Q8=makeQuery(id+"F52.imprint","IMPRINT",FACE,{"disambiguationData":[TD([[makeQuery(id+"F52.imprint","IMPRINT",EDGE,{"disambiguationData":[TD([[subQ2,-1.0]])],"derivedFrom":subQ1}),-1.0]])]});}
            extrude(context, id + "F53", {"entities" : qUnion([Q0, Q1, Q2, Q3, Q4, Q5, Q6, Q7, Q8]), "operationType" : NewBodyOperationType.REMOVE, "oppositeDirection" : true, "depth" : 381 * mm, "offsetDistance" : 25.4 * mm});
        }
        {
            var Q0;
            Q0=makeQuery(id+"F10.opExtrude","CAP_FACE",FACE,{"disambiguationData":[OSD([sQuery(id+"F8.wireOp",EDGE,"E60"),sQuery(id+"F8.wireOp",EDGE,"E97"),sQuery(id+"F8.wireOp",EDGE,"E116"),sQuery(id+"F8.wireOp",EDGE,"E308"),sQuery(id+"F8.wireOp",EDGE,"E309")])],"isStart":false});
            var sketch = newSketch(context, id + "F54", { "sketchPlane" : qUnion([Q0])});
            skLineSegment(sketch, "E373.0.0", {"start": v(19343.04, -79649.24) * mm, "end": v(18750.43, -79506.33) * mm});
            skLineSegment(sketch, "E373.0.1", {"start": v(18750.43, -79506.33) * mm, "end": v(18214.53, -81728.63) * mm});
            skLineSegment(sketch, "E373.0.2", {"start": v(18214.53, -81728.63) * mm, "end": v(18807.15, -81871.54) * mm});
            skLineSegment(sketch, "E373.0.3", {"start": v(18807.15, -81871.54) * mm, "end": v(19343.04, -79649.24) * mm});
            skLineSegment(sketch, "E374", {"start": v(18510.84, -81800.09) * mm, "end": v(19046.74, -79577.79) * mm});
            skSolve(sketch);
        }
        {
            var Q0;
            {var subQ0=sQuery(id+"F54.wireOp",EDGE,"E373.0.1");Q0=makeQuery(id+"F54.imprint","IMPRINT",FACE,{"disambiguationData":[TD([[makeQuery(id+"F54.imprint","IMPRINT",EDGE,{"derivedFrom":subQ0}),1.0]])]});}
            extrude(context, id + "F55", {"entities" : qUnion([Q0]), "operationType" : NewBodyOperationType.ADD, "depth" : 1524 * mm, "offsetDistance" : 25.4 * mm, "hasSecondDirection" : true, "secondDirectionOppositeDirection" : true, "secondDirectionDepth" : -406.4 * mm});
        }
    });
